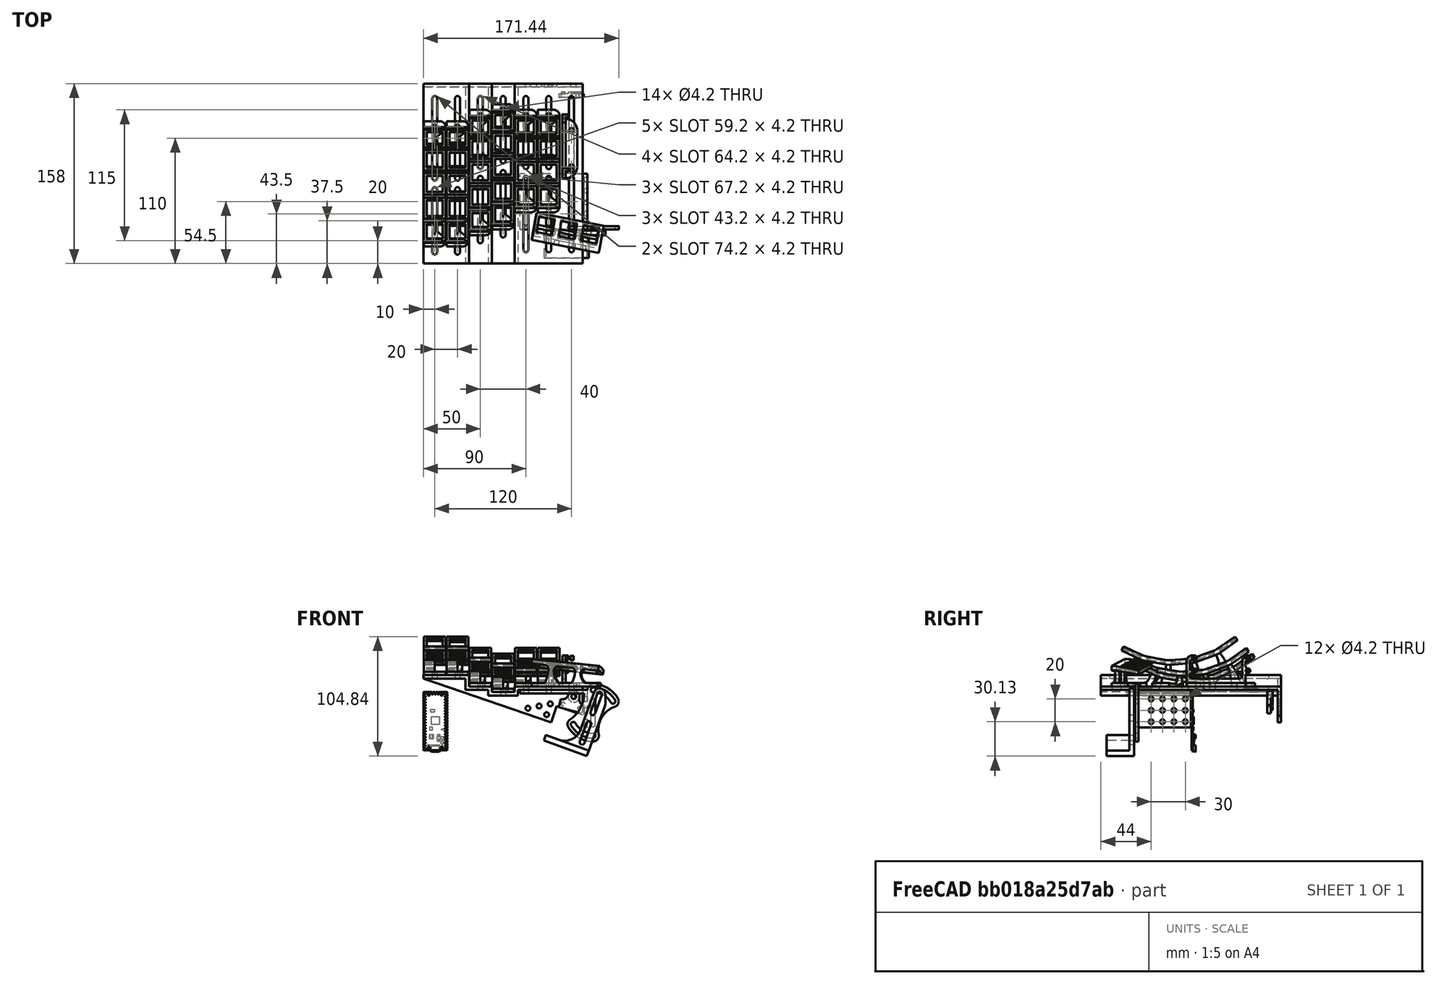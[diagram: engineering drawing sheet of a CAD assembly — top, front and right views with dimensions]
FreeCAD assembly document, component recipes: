
FREECAD ASSEMBLY — COMPONENT RECIPES ("Dactyl Chimera V3")

This assembly document has 15 components, labeled P0..P14 below (a component is one placed body or linked part). 14 of them carry a construction recipe — the FreeCAD feature program that regenerates the part from scratch, quoted from this document or its linked companion documents; the rest are supplied as boundary geometry only. No exploded tour is included for this assembly.
NOTE — document 3 of 4 of this assembly tour. The two overview renders and the header above are repeated from document 1; the component sections below continue where the previous document stopped.
COMPONENT P4 — recipe-attached ("IndexArch", modeled in this document).
Construction recipe (the document's own serialized feature program — sketch geometry with constraints, then the solid features built on it; lengths are millimeters unless a unit is written):

FEATURE [Sketcher::SketchObject] Sketch026
  FullyConstrained = true
  MapMode = 5
  Placement = pos=(0,0,0) rot=(0.57735,0.57735,0.57735;2.0944rad)
  Support = -> [YZ_Plane004]
  expr: Constraints[136] = <<Spreadsheet>>.Wiring
  expr: Constraints[56] = <<Spreadsheet>>.ZRowKey
  expr: Constraints[57] = <<Spreadsheet>>.ARowKey
  expr: Constraints[58] = <<Spreadsheet>>.QRowKey
  expr: Constraints[59] = <<Spreadsheet>>.TopRowKey
  sketch-geometry (49):
    g0: LineSegment StartX=47.4802 StartY=33.7107 StartZ=0 EndX=39.6982 EndY=28.2617 EndZ=0
    g1: LineSegment StartX=39.6982 StartY=28.2617 StartZ=0 EndX=31.9163 EndY=22.8128 EndZ=0
    g2: LineSegment StartX=31.9163 StartY=22.8128 StartZ=0 EndX=29.7273 EndY=21.6733 EndZ=0
    g3: LineSegment StartX=29.7273 StartY=21.6733 StartZ=0 EndX=20.8002 EndY=18.4241 EndZ=0
    g4: LineSegment StartX=20.8002 StartY=18.4241 StartZ=0 EndX=11.8732 EndY=15.1749 EndZ=0
    g5: LineSegment StartX=11.8732 StartY=15.1749 StartZ=0 EndX=9.46385 EndY=14.6407 EndZ=0
    g6: LineSegment StartX=9.46385 StartY=14.6407 StartZ=0 EndX=0 EndY=13.8128 EndZ=0
    g7: LineSegment StartX=0 StartY=13.8128 StartZ=0 EndX=-9.46385 EndY=12.9848 EndZ=0
    g8: LineSegment StartX=-9.46385 StartY=12.9848 StartZ=0 EndX=-11.9293 EndY=13.0924 EndZ=0
    g9: LineSegment StartX=-11.9293 StartY=13.0924 StartZ=0 EndX=-21.285 EndY=14.7421 EndZ=0
    g10: LineSegment StartX=-21.285 StartY=14.7421 StartZ=0 EndX=-30.6407 EndY=16.3917 EndZ=0
    g11: LineSegment StartX=-30.6407 StartY=16.3917 StartZ=0 EndX=-31.3353 EndY=12.4525 EndZ=0
    g12: LineSegment StartX=-31.3353 StartY=12.4525 StartZ=0 EndX=-12.6239 EndY=9.15319 EndZ=0
    g13: LineSegment StartX=-12.6239 StartY=9.15319 StartZ=0 EndX=-9.11523 EndY=9 EndZ=0
    g14: LineSegment StartX=13.2412 StartY=11.4161 StartZ=0 EndX=31.0954 EndY=17.9145 EndZ=0
    g15: LineSegment StartX=31.0954 StartY=17.9145 StartZ=0 EndX=34.2106 EndY=19.5362 EndZ=0
    g16: LineSegment StartX=-9.11523 StartY=9 StartZ=0 EndX=9.81247 EndY=10.656 EndZ=0
    g17: LineSegment StartX=9.81247 StartY=10.656 StartZ=0 EndX=13.2412 EndY=11.4161 EndZ=0
    g18: LineSegment StartX=34.2106 StartY=19.5362 StartZ=0 EndX=49.7745 EndY=30.4341 EndZ=0
    g19: LineSegment StartX=49.7745 StartY=30.4341 StartZ=0 EndX=47.4802 EndY=33.7107 EndZ=0
    g20: LineSegment StartX=31.9163 StartY=22.8128 StartZ=0 EndX=34.2106 EndY=19.5362 EndZ=0
    g21: LineSegment StartX=29.7273 StartY=21.6733 StartZ=0 EndX=31.0954 EndY=17.9145 EndZ=0
    g22: LineSegment StartX=11.8732 StartY=15.1749 StartZ=0 EndX=13.2412 EndY=11.4161 EndZ=0
    g23: LineSegment StartX=9.81247 StartY=10.656 StartZ=0 EndX=9.46385 EndY=14.6407 EndZ=0
    g24: LineSegment StartX=-9.46385 StartY=12.9848 StartZ=0 EndX=-9.11523 EndY=9 EndZ=0
    g25: LineSegment StartX=-12.6239 StartY=9.15319 StartZ=0 EndX=-11.9293 EndY=13.0924 EndZ=0
    g26: LineSegment StartX=-21.285 StartY=14.7421 StartZ=0 EndX=-20.4167 EndY=19.6661 EndZ=0
    g27: LineSegment StartX=-20.4167 StartY=19.6661 StartZ=0 EndX=-17.4623 EndY=19.1452 EndZ=0
    g28: LineSegment StartX=-17.4623 StartY=19.1452 StartZ=0 EndX=-15.7258 EndY=28.9933 EndZ=0
    g29: LineSegment StartX=-4.29592 StartY=28.4942 StartZ=0 EndX=-3.42436 EndY=18.5323 EndZ=0
    g30: LineSegment StartX=-3.42436 StartY=18.5323 StartZ=0 EndX=-0.435779 EndY=18.7937 EndZ=0
    g31: LineSegment StartX=-0.435779 StartY=18.7937 StartZ=0 EndX=0 EndY=13.8128 EndZ=0
    g32: LineSegment StartX=-0.435779 StartY=18.7937 StartZ=0 EndX=2.55281 EndY=19.0552 EndZ=0
    g33: LineSegment StartX=2.55281 StartY=19.0552 StartZ=0 EndX=1.68125 EndY=29.0171 EndZ=0
    g34: LineSegment StartX=12.8509 StartY=31.4934 StartZ=0 EndX=16.2711 EndY=22.0965 EndZ=0
    g35: LineSegment StartX=16.2711 StartY=22.0965 StartZ=0 EndX=19.0901 EndY=23.1225 EndZ=0
    g36: LineSegment StartX=19.0901 StartY=23.1225 StartZ=0 EndX=20.8002 EndY=18.4241 EndZ=0
    g37: LineSegment StartX=19.0901 StartY=23.1225 StartZ=0 EndX=21.9092 EndY=24.1486 EndZ=0
    g38: LineSegment StartX=21.9092 StartY=24.1486 StartZ=0 EndX=18.489 EndY=33.5455 EndZ=0
    g39: LineSegment StartX=28.6371 StartY=38.8283 StartZ=0 EndX=34.3729 EndY=30.6368 EndZ=0
    g40: LineSegment StartX=34.3729 StartY=30.6368 StartZ=0 EndX=36.8304 EndY=32.3575 EndZ=0
    g41: LineSegment StartX=36.8304 StartY=32.3575 StartZ=0 EndX=39.6982 EndY=28.2617 EndZ=0
    g42: ArcOfCircle CenterX=-8.11558 CenterY=72.1532 CenterZ=0 NormalX=0 NormalY=0 NormalZ=1 AngleXU=0 Radius=43.8257 StartAngle=4.53786 EndAngle=4.79966
    g43: ArcOfCircle CenterX=-2.13841 CenterY=72.6761 CenterZ=0 NormalX=0 NormalY=0 NormalZ=1 AngleXU=0 Radius=43.8257 StartAngle=4.79966 EndAngle=5.06145
    g44: ArcOfCircle CenterX=3.49974 CenterY=74.7282 CenterZ=0 NormalX=0 NormalY=0 NormalZ=1 AngleXU=0 Radius=43.8257 StartAngle=5.06145 EndAngle=5.32325
    g45: LineSegment StartX=-50 StartY=3 StartZ=0 EndX=-70 EndY=3 EndZ=0
    g46: LineSegment StartX=-50 StartY=3 StartZ=0 EndX=-50 EndY=9 EndZ=0
    g47: LineSegment StartX=-50 StartY=3 StartZ=0 EndX=-50 EndY=0 EndZ=0
    g48: LineSegment StartX=-50 StartY=9 StartZ=0 EndX=50 EndY=9 EndZ=0
  constraints (142):
    c: Coincident(g0,g1)
    c: Coincident(g1,g2)
    c: Coincident(g2,g3)
    c: Coincident(g3,g4)
    c: Coincident(g4,g5)
    c: Coincident(g5,g6)
    c: Coincident(g6,g7)
    c: Coincident(g7,g8)
    c: Coincident(g8,g9)
    c: Coincident(g9,g10)
    c: Coincident(g10,g11)
    c: Coincident(g11,g12)
    c: Coincident(g12,g13)
    c: Coincident(g14,g15)
    c: Coincident(g13,g16)
    c: Coincident(g16,g17)
    c: Coincident(g17,g14)
    c: Coincident(g15,g18)
    c: Coincident(g18,g19)
    c: Coincident(g19,g0)
    c: Coincident(g20,g1)
    c: Coincident(g20,g15)
    c: Coincident(g21,g2)
    c: Coincident(g21,g14)
    c: Coincident(g22,g4)
    c: Coincident(g22,g14)
    c: Coincident(g23,g16)
    c: Coincident(g23,g5)
    c: Coincident(g24,g7)
    c: Coincident(g24,g13)
    c: Coincident(g25,g12)
    c: Coincident(g25,g8)
    c: Coincident(g9,g26)
    c: Coincident(g26,g27)
    c: Coincident(g27,g28)
    c: Coincident(g29,g30)
    c: Coincident(g30,g31)
    c: Coincident(g31,g6)
    c: Coincident(g30,g32)
    c: Coincident(g32,g33)
    c: Coincident(g34,g35)
    c: Coincident(g35,g36)
    c: Coincident(g36,g3)
    c: Coincident(g35,g37)
    c: Coincident(g37,g38)
    c: Coincident(g39,g40)
    c: Coincident(g40,g41)
    c: Coincident(g0,g41)
    c: Angle(g41,g19) = 0
    c: Angle(g41,g20) = 0
    c: Angle(g21,g36) = 0
    c: Angle(g22,g36) = 0
    c: Angle(g23,g31) = 0
    c: Angle(g24,g31) = 0
    c: Angle(g26,g25) = 0
    c: Angle(g11,g26) = 0
    c: Distance(g26) = 5
    c: Distance(g31) = 5
    c: Distance(g36) = 5
    c: Distance(g41) = 5
    c: Angle(g1,g0) = 3.14159
    c: Angle(g3,g4) = 3.14159
    c: Angle(g6,g7) = 3.14159
    c: Angle(g10,g9) = 3.14159
    c: Perpendicular(g31,g30)
    c: Perpendicular(g30,g29)
    c: Perpendicular(g31,g32)
    c: Perpendicular(g33,g32)
    c: Distance(g16) = 19
    c: Distance(g30,g26) = 20
    c: Distance(g30,g35) = 20
    c: Distance(g35,g40) = 20
    c: Equal(g16,g12)
    c: Equal(g12,g14)
    c: Equal(g14,g18)
    c: Equal(g7,g6)
    c: Equal(g9,g10)
    c: Equal(g3,g4)
    c: Equal(g0,g1)
    c: Distance(g24) = 4
    c: Perpendicular(g31,g7)
    c: Perpendicular(g9,g26)
    c: Perpendicular(g1,g41)
    c: Equal(g20,g21)
    c: Equal(g22,g23)
    c: Equal(g25,g24)
    c: Perpendicular(g24,g16)
    c: Perpendicular(g14,g22)
    c: Perpendicular(g22,g4)
    c: Perpendicular(g20,g18)
    c: Angle(g35,g37) = 3.14159
    c: Perpendicular(g36,g37)
    c: Perpendicular(g37,g38)
    c: Perpendicular(g34,g35)
    c: Perpendicular(g26,g27)
    c: Coincident(g42,g28)
    c: Coincident(g42,g29)
    c: Coincident(g43,g33)
    c: Coincident(g43,g34)
    c: Coincident(g44,g38)
    c: Coincident(g44,g39)
    c: Perpendicular(g44,g38)
    c: Perpendicular(g44,g39)
    c: Perpendicular(g43,g34)
    c: Perpendicular(g43,g33)
    c: Perpendicular(g42,g29)
    c: Perpendicular(g42,g28)
    c: Perpendicular(g27,g28)
    c: Perpendicular(g12,g25)
    c: Equal(g27,g30)
    c: Equal(g30,g32)
    c: Equal(g32,g35)
    c: Equal(g35,g37)
    c: Equal(g37,g40)
    c: Perpendicular(g41,g40)
    c: Distance(g32) = 3
    c: Perpendicular(g39,g40)
    c: Distance(g28) = 10
    c: Distance(g29) = 10
    c: Distance(g33) = 10
    c: Distance(g34) = 10
    c: Distance(g38) = 10
    c: Distance(g39) = 10
    c: Angle(g26,g31) = 0.261799
    c: Angle(g31,g36) = 0.261799
    c: Angle(g36,g41) = 0.261799
    c: Angle(g45,g31) = 1.65806
    c: Coincident(g46,g45)
    c: Vertical(g46)
    c: Coincident(g47,g45)
    c: PointOnObject(g47,g-1)
    c: Vertical(g47)
    c: Coincident(g48,g46)
    c: Horizontal(g48)
    c: Horizontal(g45)
    c: DistanceY(g47,g47) = 3
    c: DistanceY(g46,g46) = 6
    c: DistanceX(g45,g45) = 20
    c: DistanceX(g47,g-1) = 50
    c: DistanceX(g48,g48) = 100
    c: PointOnObject(g6,g-2)
    c: PointOnObject(g13,g48)
FEATURE [PartDesign::Pad] Pad016  label="IArch"
  Direction = (1,-2e-16,3e-16)
  Length = 19
  Length2 = 10
  Midplane = true
  Placement = pos=(0,0,0) rot=(0.57735,0.57735,0.57735;2.0944rad)
  Profile = -> Sketch026
  ReferenceAxis = -> Sketch026 [N_Axis]
  Type = 0
FEATURE [Sketcher::SketchObject] Sketch027
  ExternalGeometry = -> [Sketch026]
  FullyConstrained = true
  MapMode = 5
  Placement = pos=(0,0,0) rot=(0.57735,0.57735,0.57735;2.0944rad)
  Support = -> [YZ_Plane004]
  sketch-geometry (60):
    g0: LineSegment StartX=-21.285 StartY=14.7421 StartZ=0 EndX=-21.9796 EndY=10.8028 EndZ=0
    g1: LineSegment StartX=0 StartY=13.8128 StartZ=0 EndX=0.348623 EndY=9.82798 EndZ=0
    g2: LineSegment StartX=20.8002 StartY=18.4241 StartZ=0 EndX=22.1683 EndY=14.6653 EndZ=0
    g3: LineSegment StartX=39.6982 StartY=28.2617 StartZ=0 EndX=41.9925 EndY=24.9851 EndZ=0
    g4: LineSegment StartX=-28.1786 StartY=15.9576 StartZ=0 EndX=-21.285 EndY=14.7421 EndZ=0
    g5: LineSegment StartX=-21.285 StartY=14.7421 StartZ=0 EndX=-14.3913 EndY=13.5265 EndZ=0
    g6: LineSegment StartX=-14.3913 StartY=13.5265 StartZ=0 EndX=-14.6344 EndY=12.1478 EndZ=0
    g7: LineSegment StartX=-14.6344 StartY=12.1478 StartZ=0 EndX=-13.3542 EndY=11.9221 EndZ=0
    g8: LineSegment StartX=-13.3542 StartY=11.9221 StartZ=0 EndX=-13.8057 EndY=9.36157 EndZ=0
    g9: LineSegment StartX=-13.8057 StartY=9.36157 StartZ=0 EndX=-21.9796 EndY=10.8028 EndZ=0
    g10: LineSegment StartX=-21.9796 StartY=10.8028 StartZ=0 EndX=-30.1535 EndY=12.2441 EndZ=0
    g11: LineSegment StartX=-30.1535 StartY=12.2441 StartZ=0 EndX=-29.702 EndY=14.8046 EndZ=0
    g12: LineSegment StartX=-29.702 StartY=14.8046 StartZ=0 EndX=-28.4217 EndY=14.5789 EndZ=0
    g13: LineSegment StartX=-28.4217 StartY=14.5789 StartZ=0 EndX=-28.1786 EndY=15.9576 EndZ=0
    g14: LineSegment StartX=-29.702 StartY=14.8046 StartZ=0 EndX=-29.4589 EndY=16.1834 EndZ=0
    g15: LineSegment StartX=-13.3542 StartY=11.9221 StartZ=0 EndX=-13.1111 EndY=13.3008 EndZ=0
    g16: LineSegment StartX=-14.6344 StartY=12.1478 StartZ=0 EndX=-15.0859 EndY=9.58731 EndZ=0
    g17: LineSegment StartX=-28.4217 StartY=14.5789 StartZ=0 EndX=-28.8732 EndY=12.0184 EndZ=0
    g18: LineSegment StartX=-6.97336 StartY=13.2027 StartZ=0 EndX=0 EndY=13.8128 EndZ=0
    g19: LineSegment StartX=0 StartY=13.8128 StartZ=0 EndX=6.97336 EndY=14.4228 EndZ=0
    g20: LineSegment StartX=6.97336 StartY=14.4228 StartZ=0 EndX=7.09538 EndY=13.0282 EndZ=0
    g21: LineSegment StartX=7.09538 StartY=13.0282 StartZ=0 EndX=8.39043 EndY=13.1415 EndZ=0
    g22: LineSegment StartX=8.39043 StartY=13.1415 StartZ=0 EndX=8.61704 EndY=10.5514 EndZ=0
    g23: LineSegment StartX=8.61704 StartY=10.5514 StartZ=0 EndX=0.348623 EndY=9.82798 EndZ=0
    g24: LineSegment StartX=0.348623 StartY=9.82798 StartZ=0 EndX=-7.91979 EndY=9.10459 EndZ=0
    g25: LineSegment StartX=-7.91979 StartY=9.10459 StartZ=0 EndX=-8.1464 EndY=11.6947 EndZ=0
    g26: LineSegment StartX=-8.1464 StartY=11.6947 StartZ=0 EndX=-6.85134 EndY=11.808 EndZ=0
    g27: LineSegment StartX=-6.85134 StartY=11.808 StartZ=0 EndX=-6.97336 EndY=13.2027 EndZ=0
    g28: LineSegment StartX=14.2224 StartY=16.0299 StartZ=0 EndX=20.8002 EndY=18.4241 EndZ=0
    g29: LineSegment StartX=20.8002 StartY=18.4241 StartZ=0 EndX=27.3781 EndY=20.8182 EndZ=0
    g30: LineSegment StartX=27.3781 StartY=20.8182 StartZ=0 EndX=27.8569 EndY=19.5026 EndZ=0
    g31: LineSegment StartX=27.8569 StartY=19.5026 StartZ=0 EndX=29.0785 EndY=19.9473 EndZ=0
    g32: LineSegment StartX=29.0785 StartY=19.9473 StartZ=0 EndX=29.9678 EndY=17.5041 EndZ=0
    g33: LineSegment StartX=29.9678 StartY=17.5041 StartZ=0 EndX=22.1683 EndY=14.6653 EndZ=0
    g34: LineSegment StartX=22.1683 StartY=14.6653 StartZ=0 EndX=14.3689 EndY=11.8265 EndZ=0
    g35: LineSegment StartX=14.3689 StartY=11.8265 StartZ=0 EndX=13.4796 EndY=14.2697 EndZ=0
    g36: LineSegment StartX=13.4796 StartY=14.2697 StartZ=0 EndX=14.7012 EndY=14.7144 EndZ=0
    g37: LineSegment StartX=14.7012 StartY=14.7144 StartZ=0 EndX=14.2224 EndY=16.0299 EndZ=0
    g38: LineSegment StartX=33.9642 StartY=24.2467 StartZ=0 EndX=39.6982 EndY=28.2617 EndZ=0
    g39: LineSegment StartX=39.6982 StartY=28.2617 StartZ=0 EndX=45.4323 EndY=32.2768 EndZ=0
    g40: LineSegment StartX=45.4323 StartY=32.2768 StartZ=0 EndX=46.2353 EndY=31.13 EndZ=0
    g41: LineSegment StartX=46.2353 StartY=31.13 StartZ=0 EndX=47.3002 EndY=31.8756 EndZ=0
    g42: LineSegment StartX=47.3002 StartY=31.8756 StartZ=0 EndX=48.7915 EndY=29.7458 EndZ=0
    g43: LineSegment StartX=48.7915 StartY=29.7458 StartZ=0 EndX=41.9925 EndY=24.9851 EndZ=0
    g44: LineSegment StartX=41.9925 StartY=24.9851 StartZ=0 EndX=35.1936 EndY=20.2244 EndZ=0
    g45: LineSegment StartX=35.1936 StartY=20.2244 StartZ=0 EndX=33.7023 EndY=22.3542 EndZ=0
    g46: LineSegment StartX=33.7023 StartY=22.3542 StartZ=0 EndX=34.7672 EndY=23.0999 EndZ=0
    g47: LineSegment StartX=34.7672 StartY=23.0999 StartZ=0 EndX=33.9642 EndY=24.2467 EndZ=0
    g48: LineSegment StartX=-8.1464 StartY=11.6947 StartZ=0 EndX=-8.26842 EndY=13.0894 EndZ=0
    g49: LineSegment StartX=-6.85134 StartY=11.808 StartZ=0 EndX=-6.62474 EndY=9.21789 EndZ=0
    g50: LineSegment StartX=7.09538 StartY=13.0282 StartZ=0 EndX=7.32199 EndY=10.4381 EndZ=0
    g51: LineSegment StartX=8.39043 StartY=13.1415 StartZ=0 EndX=8.26842 EndY=14.5362 EndZ=0
    g52: LineSegment StartX=14.7012 StartY=14.7144 StartZ=0 EndX=15.5905 EndY=12.2711 EndZ=0
    g53: LineSegment StartX=13.4796 StartY=14.2697 StartZ=0 EndX=13.0008 EndY=15.5853 EndZ=0
    g54: LineSegment StartX=27.8569 StartY=19.5026 StartZ=0 EndX=28.7462 EndY=17.0594 EndZ=0
    g55: LineSegment StartX=29.0785 StartY=19.9473 StartZ=0 EndX=28.5997 EndY=21.2628 EndZ=0
    g56: LineSegment StartX=34.7672 StartY=23.0999 StartZ=0 EndX=36.2585 EndY=20.9701 EndZ=0
    g57: LineSegment StartX=33.7023 StartY=22.3542 StartZ=0 EndX=32.8993 EndY=23.5011 EndZ=0
    g58: LineSegment StartX=46.2353 StartY=31.13 StartZ=0 EndX=47.7266 EndY=29.0002 EndZ=0
    g59: LineSegment StartX=47.3002 StartY=31.8756 StartZ=0 EndX=46.4972 EndY=33.0224 EndZ=0
  constraints (172):
    c: Coincident(g0,g-4)
    c: PointOnObject(g0,g-5)
    c: Coincident(g1,g-8)
    c: PointOnObject(g1,g-6)
    c: Coincident(g2,g-10)
    c: PointOnObject(g2,g-11)
    c: Coincident(g3,g-14)
    c: PointOnObject(g3,g-12)
    c: Perpendicular(g-12,g3)
    c: Perpendicular(g-11,g2)
    c: Perpendicular(g-6,g1)
    c: Perpendicular(g-5,g0)
    c: PointOnObject(g4,g-3)
    c: Coincident(g4,g0)
    c: Coincident(g4,g5)
    c: PointOnObject(g5,g-4)
    c: Coincident(g5,g6)
    c: Coincident(g6,g7)
    c: Coincident(g7,g8)
    c: PointOnObject(g8,g-5)
    c: Coincident(g8,g9)
    c: Coincident(g9,g0)
    c: Coincident(g9,g10)
    c: PointOnObject(g10,g-5)
    c: Coincident(g10,g11)
    c: Coincident(g11,g12)
    c: Coincident(g12,g13)
    c: Coincident(g13,g4)
    c: Coincident(g14,g11)
    c: PointOnObject(g14,g-3)
    c: Coincident(g15,g7)
    c: PointOnObject(g15,g-4)
    c: Coincident(g16,g6)
    c: PointOnObject(g16,g9)
    c: Coincident(g17,g12)
    c: PointOnObject(g17,g10)
    c: Angle(g15,g8) = 3.14159
    c: Angle(g16,g6) = 3.14159
    c: Angle(g17,g13) = 3.14159
    c: Angle(g11,g14) = 3.14159
    c: Distance(g8,g10) = 16.6
    c: Distance(g4,g5) = 14
    c: Equal(g5,g4)
    c: Equal(g9,g10)
    c: Perpendicular(g4,g13)
    c: Distance(g13) = 1.4
    c: Equal(g14,g13)
    c: Equal(g13,g6)
    c: Equal(g6,g15)
    c: Perpendicular(g10,g11)
    c: Perpendicular(g5,g6)
    c: Perpendicular(g9,g8)
    c: PointOnObject(g18,g-7)
    c: Coincident(g18,g1)
    c: Coincident(g18,g19)
    c: PointOnObject(g19,g-8)
    c: Coincident(g19,g20)
    c: Coincident(g20,g21)
    c: Coincident(g21,g22)
    c: PointOnObject(g22,g-6)
    c: Coincident(g22,g23)
    c: Coincident(g23,g1)
    c: Coincident(g23,g24)
    c: PointOnObject(g24,g-6)
    c: Coincident(g24,g25)
    c: Coincident(g25,g26)
    c: Coincident(g26,g27)
    c: Coincident(g27,g18)
    c: PointOnObject(g28,g-9)
    c: Coincident(g28,g2)
    c: Coincident(g28,g29)
    c: PointOnObject(g29,g-10)
    c: Coincident(g29,g30)
    c: Coincident(g30,g31)
    c: Coincident(g31,g32)
    c: PointOnObject(g32,g-11)
    c: Coincident(g32,g33)
    c: Coincident(g33,g2)
    c: Coincident(g33,g34)
    c: PointOnObject(g34,g-11)
    c: Coincident(g34,g35)
    c: Coincident(g35,g36)
    c: Coincident(g36,g37)
    c: Coincident(g37,g28)
    c: Coincident(g38,g3)
    c: Coincident(g38,g39)
    c: PointOnObject(g39,g-13)
    c: Coincident(g39,g40)
    c: Coincident(g40,g41)
    c: Coincident(g41,g42)
    c: PointOnObject(g42,g-12)
    c: Coincident(g42,g43)
    c: Coincident(g43,g3)
    c: Coincident(g43,g44)
    c: PointOnObject(g44,g-12)
    c: Coincident(g44,g45)
    c: Coincident(g45,g46)
    c: Coincident(g46,g47)
    c: Coincident(g47,g38)
    c: PointOnObject(g38,g-14)
    c: Equal(g19,g18)
    c: Equal(g28,g29)
    c: Equal(g38,g39)
    c: Equal(g24,g23)
    c: Equal(g34,g33)
    c: Equal(g44,g43)
    c: Distance(g24,g22) = 16.6
    c: Distance(g34,g32) = 16.6
    c: Distance(g44,g42) = 16.6
    c: Distance(g39,g38) = 14
    c: Distance(g29,g28) = 14
    c: Distance(g19,g18) = 14
    c: Coincident(g48,g25)
    c: PointOnObject(g48,g-7)
    c: Coincident(g49,g26)
    c: PointOnObject(g49,g24)
    c: Coincident(g50,g20)
    c: Coincident(g51,g21)
    c: PointOnObject(g51,g-8)
    c: Coincident(g52,g36)
    c: PointOnObject(g52,g34)
    c: Coincident(g53,g35)
    c: PointOnObject(g53,g-9)
    c: PointOnObject(g54,g33)
    c: Coincident(g55,g31)
    c: PointOnObject(g55,g-10)
    c: Coincident(g56,g46)
    c: PointOnObject(g56,g44)
    c: Coincident(g57,g45)
    c: PointOnObject(g57,g-14)
    c: Coincident(g58,g40)
    c: PointOnObject(g58,g43)
    c: Coincident(g59,g41)
    c: PointOnObject(g59,g-13)
    c: Coincident(g54,g30)
    c: Angle(g32,g55) = 3.14159
    c: Angle(g25,g48) = 3.14159
    c: Angle(g27,g49) = 3.14159
    c: Angle(g50,g20) = 3.14159
    c: Angle(g22,g51) = 3.14159
    c: Angle(g35,g53) = 3.14159
    c: Angle(g52,g37) = 3.14159
    c: Angle(g54,g30) = 3.14159
    c: Angle(g45,g57) = 3.14159
    c: Angle(g47,g56) = 3.14159
    c: Angle(g58,g40) = 3.14159
    c: Angle(g42,g59) = 3.14159
    c: Perpendicular(g24,g25)
    c: Perpendicular(g18,g27)
    c: Perpendicular(g19,g20)
    c: Perpendicular(g23,g22)
    c: Perpendicular(g28,g37)
    c: Perpendicular(g34,g35)
    c: Perpendicular(g29,g30)
    c: Perpendicular(g33,g32)
    c: Perpendicular(g44,g45)
    c: Perpendicular(g39,g40)
    c: Perpendicular(g43,g42)
    c: Equal(g59,g40)
    c: Equal(g40,g47)
    c: Equal(g47,g57)
    c: Equal(g55,g30)
    c: Equal(g30,g37)
    c: Equal(g37,g53)
    c: Equal(g51,g20)
    c: Equal(g20,g27)
    c: Equal(g27,g48)
    c: Distance(g48) = 1.4
    c: PointOnObject(g50,g23)
    c: Distance(g53) = 1.4
    c: Distance(g57) = 1.4
    c: Perpendicular(g38,g47)
FEATURE [PartDesign::Pocket] Pocket008  label="IMX Sockets"
  BaseFeature = -> Pad016
  Direction = (-1,2e-16,-3e-16)
  Length = 14
  Length2 = 5
  Midplane = true
  Placement = pos=(0,0,0) rot=(0.57735,0.57735,0.57735;2.0944rad)
  Profile = -> Sketch027
  ReferenceAxis = -> Sketch027 [N_Axis]
  Type = 0
FEATURE [Sketcher::SketchObject] Sketch028
  ExternalGeometry = -> [Sketch027]
  FullyConstrained = true
  MapMode = 5
  Placement = pos=(0,0,0) rot=(0.57735,0.57735,0.57735;2.0944rad)
  Support = -> [YZ_Plane004]
  sketch-geometry (44):
    g0: LineSegment StartX=-21.285 StartY=14.7421 StartZ=0 EndX=-21.4934 EndY=13.5603 EndZ=0
    g1: LineSegment StartX=-21.4934 StartY=13.5603 StartZ=0 EndX=-21.667 EndY=12.5755 EndZ=0
    g2: LineSegment StartX=-21.667 StartY=12.5755 StartZ=0 EndX=-21.9796 EndY=10.8028 EndZ=0
    g3: LineSegment StartX=0 StartY=13.8128 StartZ=0 EndX=0.104587 EndY=12.6173 EndZ=0
    g4: LineSegment StartX=0.104587 StartY=12.6173 StartZ=0 EndX=0.191743 EndY=11.6211 EndZ=0
    g5: LineSegment StartX=0.191743 StartY=11.6211 StartZ=0 EndX=0.348623 EndY=9.82798 EndZ=0
    g6: LineSegment StartX=39.6982 StartY=28.2617 StartZ=0 EndX=40.3865 EndY=27.2788 EndZ=0
    g7: LineSegment StartX=40.3865 StartY=27.2788 StartZ=0 EndX=40.9601 EndY=26.4596 EndZ=0
    g8: LineSegment StartX=40.9601 StartY=26.4596 StartZ=0 EndX=41.9925 EndY=24.9851 EndZ=0
    g9: LineSegment StartX=22.1683 StartY=14.6653 StartZ=0 EndX=21.5527 EndY=16.3567 EndZ=0
    g10: LineSegment StartX=21.5527 StartY=16.3567 StartZ=0 EndX=21.2107 EndY=17.2964 EndZ=0
    g11: LineSegment StartX=21.2107 StartY=17.2964 StartZ=0 EndX=20.8002 EndY=18.4241 EndZ=0
    g12: LineSegment StartX=-28.387 StartY=14.7758 StartZ=0 EndX=-14.5997 EndY=12.3448 EndZ=0
    g13: LineSegment StartX=-14.5997 StartY=12.3448 StartZ=0 EndX=-14.6344 EndY=12.1478 EndZ=0
    g14: LineSegment StartX=-14.6344 StartY=12.1478 StartZ=0 EndX=-13.3542 EndY=11.9221 EndZ=0
    g15: LineSegment StartX=-13.3542 StartY=11.9221 StartZ=0 EndX=-13.4931 EndY=11.1342 EndZ=0
    g16: LineSegment StartX=-13.4931 StartY=11.1342 StartZ=0 EndX=-29.8409 EndY=14.0168 EndZ=0
    g17: LineSegment StartX=-29.8409 StartY=14.0168 StartZ=0 EndX=-29.702 EndY=14.8046 EndZ=0
    g18: LineSegment StartX=-29.702 StartY=14.8046 StartZ=0 EndX=-28.4217 EndY=14.5789 EndZ=0
    g19: LineSegment StartX=-28.4217 StartY=14.5789 StartZ=0 EndX=-28.387 EndY=14.7758 EndZ=0
    g20: LineSegment StartX=-6.86878 StartY=12.0072 StartZ=0 EndX=7.07795 EndY=13.2274 EndZ=0
    g21: LineSegment StartX=7.07795 StartY=13.2274 StartZ=0 EndX=7.09538 EndY=13.0282 EndZ=0
    g22: LineSegment StartX=7.09538 StartY=13.0282 StartZ=0 EndX=8.39043 EndY=13.1415 EndZ=0
    g23: LineSegment StartX=8.39043 StartY=13.1415 StartZ=0 EndX=8.46016 EndY=12.3445 EndZ=0
    g24: LineSegment StartX=8.46016 StartY=12.3445 StartZ=0 EndX=-8.07667 EndY=10.8977 EndZ=0
    g25: LineSegment StartX=-8.07667 StartY=10.8977 StartZ=0 EndX=-8.1464 EndY=11.6947 EndZ=0
    g26: LineSegment StartX=-8.1464 StartY=11.6947 StartZ=0 EndX=-6.85134 EndY=11.808 EndZ=0
    g27: LineSegment StartX=-6.85134 StartY=11.808 StartZ=0 EndX=-6.86878 EndY=12.0072 EndZ=0
    g28: LineSegment StartX=14.6328 StartY=14.9023 StartZ=0 EndX=27.7885 EndY=19.6906 EndZ=0
    g29: LineSegment StartX=27.7885 StartY=19.6906 StartZ=0 EndX=27.8569 EndY=19.5026 EndZ=0
    g30: LineSegment StartX=27.8569 StartY=19.5026 StartZ=0 EndX=29.0785 EndY=19.9473 EndZ=0
    g31: LineSegment StartX=29.0785 StartY=19.9473 StartZ=0 EndX=29.3521 EndY=19.1955 EndZ=0
    g32: LineSegment StartX=29.3521 StartY=19.1955 StartZ=0 EndX=13.7532 EndY=13.518 EndZ=0
    g33: LineSegment StartX=13.7532 StartY=13.518 StartZ=0 EndX=13.4796 EndY=14.2697 EndZ=0
    g34: LineSegment StartX=13.4796 StartY=14.2697 StartZ=0 EndX=14.7012 EndY=14.7144 EndZ=0
    g35: LineSegment StartX=14.7012 StartY=14.7144 StartZ=0 EndX=14.6328 EndY=14.9023 EndZ=0
    g36: LineSegment StartX=34.6525 StartY=23.2637 StartZ=0 EndX=46.1206 EndY=31.2938 EndZ=0
    g37: LineSegment StartX=46.1206 StartY=31.2938 StartZ=0 EndX=46.2353 EndY=31.13 EndZ=0
    g38: LineSegment StartX=46.2353 StartY=31.13 StartZ=0 EndX=47.3002 EndY=31.8756 EndZ=0
    g39: LineSegment StartX=47.3002 StartY=31.8756 StartZ=0 EndX=47.7591 EndY=31.2203 EndZ=0
    g40: LineSegment StartX=47.7591 StartY=31.2203 StartZ=0 EndX=34.1611 EndY=21.6989 EndZ=0
    g41: LineSegment StartX=34.1611 StartY=21.6989 StartZ=0 EndX=33.7023 EndY=22.3542 EndZ=0
    g42: LineSegment StartX=33.7023 StartY=22.3542 StartZ=0 EndX=34.7672 EndY=23.0999 EndZ=0
    g43: LineSegment StartX=34.7672 StartY=23.0999 StartZ=0 EndX=34.6525 EndY=23.2637 EndZ=0
  constraints (112):
    c: Coincident(g-21,g0)
    c: Coincident(g0,g1)
    c: Coincident(g1,g2)
    c: Coincident(g2,g-24)
    c: Coincident(g-16,g3)
    c: Coincident(g3,g4)
    c: Coincident(g4,g5)
    c: Coincident(g5,g-15)
    c: Coincident(g-6,g6)
    c: Coincident(g6,g7)
    c: Coincident(g7,g8)
    c: Coincident(g8,g-3)
    c: Coincident(g-10,g9)
    c: Coincident(g9,g10)
    c: Coincident(g10,g11)
    c: Coincident(g11,g-9)
    c: Angle(g6,g7) = 3.14159
    c: Angle(g8,g7) = 3.14159
    c: Angle(g11,g10) = 3.14159
    c: Angle(g9,g10) = 3.14159
    c: Angle(g3,g4) = 3.14159
    c: Angle(g5,g4) = 3.14159
    c: Angle(g0,g1) = 3.14159
    c: Angle(g2,g1) = 3.14159
    c: PointOnObject(g12,g-26)
    c: PointOnObject(g12,g-22)
    c: Coincident(g12,g13)
    c: Coincident(g13,g-22)
    c: Coincident(g13,g14)
    c: Coincident(g14,g-23)
    c: Coincident(g14,g15)
    c: PointOnObject(g15,g-23)
    c: Coincident(g15,g16)
    c: PointOnObject(g16,g-25)
    c: Coincident(g16,g17)
    c: Coincident(g17,g-25)
    c: Coincident(g17,g18)
    c: Coincident(g18,g-26)
    c: Coincident(g18,g19)
    c: Coincident(g19,g12)
    c: PointOnObject(g20,g-17)
    c: PointOnObject(g20,g-19)
    c: Coincident(g20,g21)
    c: Coincident(g21,g-19)
    c: Coincident(g21,g22)
    c: Coincident(g22,g-20)
    c: Coincident(g22,g23)
    c: PointOnObject(g23,g-20)
    c: Coincident(g23,g24)
    c: PointOnObject(g24,g-18)
    c: Coincident(g24,g25)
    c: Coincident(g25,g-18)
    c: Coincident(g25,g26)
    c: Coincident(g26,g-17)
    c: Coincident(g26,g27)
    c: Coincident(g27,g20)
    c: PointOnObject(g28,g-14)
    c: PointOnObject(g28,g-12)
    c: Coincident(g28,g29)
    c: Coincident(g29,g-12)
    c: Coincident(g29,g30)
    c: Coincident(g30,g-11)
    c: Coincident(g30,g31)
    c: PointOnObject(g31,g-11)
    c: Coincident(g31,g32)
    c: Coincident(g32,g33)
    c: Coincident(g33,g-13)
    c: Coincident(g33,g34)
    c: Coincident(g34,g-14)
    c: Coincident(g34,g35)
    c: Coincident(g35,g28)
    c: PointOnObject(g36,g-7)
    c: PointOnObject(g36,g-4)
    c: Coincident(g36,g37)
    c: Coincident(g37,g-4)
    c: Coincident(g37,g38)
    c: Coincident(g38,g-5)
    c: Coincident(g38,g39)
    c: PointOnObject(g39,g-5)
    c: Coincident(g39,g40)
    c: PointOnObject(g40,g-8)
    c: Coincident(g40,g41)
    c: Coincident(g41,g-8)
    c: Coincident(g41,g42)
    c: Coincident(g42,g-7)
    c: Coincident(g42,g43)
    c: Coincident(g43,g36)
    c: PointOnObject(g32,g-13)
    c: PointOnObject(g1,g16)
    c: PointOnObject(g0,g12)
    c: PointOnObject(g3,g20)
    c: PointOnObject(g4,g24)
    c: PointOnObject(g10,g28)
    c: PointOnObject(g9,g32)
    c: PointOnObject(g6,g36)
    c: PointOnObject(g7,g40)
    c: Perpendicular(g36,g6)
    c: Perpendicular(g8,g40)
    c: Perpendicular(g9,g32)
    c: Perpendicular(g11,g28)
    c: Perpendicular(g3,g20)
    c: Perpendicular(g5,g24)
    c: Perpendicular(g2,g16)
    c: Perpendicular(g0,g12)
    c: Equal(g7,g10)
    c: Equal(g10,g4)
    c: Equal(g4,g1)
    c: Equal(g0,g3)
    c: Equal(g3,g11)
    c: Equal(g11,g6)
    c: Distance(g4) = 1
    c: Distance(g3) = 1.2
FEATURE [PartDesign::Pocket] Pocket009  label="IChoc Sockets"
  BaseFeature = -> Pocket008
  Direction = (-1,2e-16,-3e-16)
  Length = 14.6
  Length2 = 5
  Midplane = true
  Placement = pos=(0,0,0) rot=(0.57735,0.57735,0.57735;2.0944rad)
  Profile = -> Sketch028
  ReferenceAxis = -> Sketch028 [N_Axis]
  Type = 0
FEATURE [Sketcher::SketchObject] Sketch029
  ExternalGeometry = -> [Sketch026]
  FullyConstrained = true
  MapMode = 5
  Placement = pos=(0,0,0) rot=(0.57735,0.57735,0.57735;2.0944rad)
  Support = -> [YZ_Plane004]
  expr: Constraints[18] = <<Spreadsheet>>.Wiring
  sketch-geometry (8):
    g0: LineSegment StartX=9.46385 StartY=14.6407 StartZ=0 EndX=9.81247 EndY=10.656 EndZ=0
    g1: LineSegment StartX=9.81247 StartY=10.656 StartZ=0 EndX=10.3354 EndY=4.67879 EndZ=0
    g2: LineSegment StartX=10.3354 StartY=4.67879 StartZ=0 EndX=10.3354 EndY=0 EndZ=0
    g3: LineSegment StartX=10.3354 StartY=0 StartZ=0 EndX=15.2934 EndY=0 EndZ=0
    g4: LineSegment StartX=15.2934 StartY=0 StartZ=0 EndX=15.2934 EndY=5.77794 EndZ=0
    g5: LineSegment StartX=15.2934 StartY=5.77794 StartZ=0 EndX=13.2412 EndY=11.4161 EndZ=0
    g6: LineSegment StartX=13.2412 StartY=11.4161 StartZ=0 EndX=11.8732 EndY=15.1749 EndZ=0
    g7: LineSegment StartX=9.46385 StartY=14.6407 StartZ=0 EndX=11.8732 EndY=15.1749 EndZ=0
  constraints (20):
    c: Coincident(g-3,g0)
    c: Coincident(g0,g-4)
    c: Coincident(g0,g1)
    c: Coincident(g1,g2)
    c: PointOnObject(g2,g-1)
    c: Vertical(g2)
    c: Coincident(g2,g3)
    c: PointOnObject(g3,g-1)
    c: Coincident(g3,g4)
    c: Vertical(g4)
    c: Coincident(g4,g5)
    c: Coincident(g5,g-4)
    c: Coincident(g5,g6)
    c: Coincident(g6,g-3)
    c: Coincident(g7,g-3)
    c: Coincident(g7,g-3)
    c: Angle(g0,g1) = 3.14159
    c: Angle(g5,g6) = 3.14159
    c: Distance(g1) = 6
    c: Equal(g5,g1)
FEATURE [PartDesign::Pad] Pad017  label="IInner Legs"
  BaseFeature = -> Pocket009
  Direction = (1,-2e-16,3e-16)
  Length = 4.1
  Length2 = 9.5
  Placement = pos=(0,0,0) rot=(0.57735,0.57735,0.57735;2.0944rad)
  Profile = -> Sketch029
  ReferenceAxis = -> Sketch029 [N_Axis]
  Type = 4
  expr: Length = <<Spreadsheet>>.ScrewD / 2 + 2mm
  expr: Length2 = 9.5
FEATURE [Sketcher::SketchObject] Sketch030
  ExternalGeometry = -> [Sketch026]
  FullyConstrained = true
  MapMode = 5
  Placement = pos=(0,0,0) rot=(0.57735,0.57735,0.57735;2.0944rad)
  Support = -> [YZ_Plane004]
  expr: Constraints[32] = <<Spreadsheet>>.Wiring
  expr: Constraints[42] = <<Spreadsheet>>.ArchLength - 10mm
  expr: Constraints[43] = <<Spreadsheet>>.ArchLength - 30mm
  expr: Constraints[44] = <<Spreadsheet>>.ArchLength
  expr: Constraints[45] = <<Spreadsheet>>.ArchLength - 20mm
  expr: Constraints[52] = <<Spreadsheet>>.ArchLength - 25mm
  expr: Constraints[53] = <<Spreadsheet>>.ArchLength - 5mm
  sketch-geometry (36):
    g0: LineSegment StartX=-13.6658 StartY=3.24435 StartZ=0 EndX=-12.6239 EndY=9.15319 EndZ=0
    g1: LineSegment StartX=-12.6239 StartY=9.15319 StartZ=0 EndX=-11.9293 EndY=13.0924 EndZ=0
    g2: LineSegment StartX=-11.9293 StartY=13.0924 StartZ=0 EndX=-9.46385 EndY=12.9848 EndZ=0
    g3: LineSegment StartX=-9.46385 StartY=12.9848 StartZ=0 EndX=-9.11523 EndY=9 EndZ=0
    g4: LineSegment StartX=-15 StartY=0 StartZ=0 EndX=-25 EndY=0 EndZ=0
    g5: LineSegment StartX=-25 StartY=0 StartZ=0 EndX=-25 EndY=3 EndZ=0
    g6: LineSegment StartX=-9.11523 StartY=9 StartZ=0 EndX=-8.59229 EndY=3.02283 EndZ=0
    g7: LineSegment StartX=-8.59229 StartY=3.02283 StartZ=0 EndX=-15 EndY=0 EndZ=0
    g8: LineSegment StartX=37.6521 StartY=14.6212 StartZ=0 EndX=34.2106 EndY=19.5362 EndZ=0
    g9: LineSegment StartX=34.2106 StartY=19.5362 StartZ=0 EndX=31.9163 EndY=22.8128 EndZ=0
    g10: LineSegment StartX=31.9163 StartY=22.8128 StartZ=0 EndX=29.7273 EndY=21.6733 EndZ=0
    g11: LineSegment StartX=29.7273 StartY=21.6733 StartZ=0 EndX=31.0954 EndY=17.9145 EndZ=0
    g12: LineSegment StartX=31.0954 StartY=17.9145 StartZ=0 EndX=33.1475 EndY=12.2763 EndZ=0
    g13: LineSegment StartX=33.1475 StartY=12.2763 StartZ=0 EndX=35 EndY=0 EndZ=0
    g14: LineSegment StartX=35 StartY=0 StartZ=0 EndX=45 EndY=0 EndZ=0
    g15: LineSegment StartX=45 StartY=0 StartZ=0 EndX=45 EndY=3 EndZ=0
    g16: LineSegment StartX=-13.6658 StartY=3.24435 StartZ=0 EndX=-13.9496 EndY=1.63459 EndZ=0
    g17: LineSegment StartX=-13.9496 StartY=1.63459 StartZ=0 EndX=-13.9496 EndY=0 EndZ=0
    g18: LineSegment StartX=45 StartY=3 StartZ=0 EndX=40 EndY=3 EndZ=0
    g19: LineSegment StartX=-25 StartY=3 StartZ=0 EndX=-20 EndY=3 EndZ=0
    g20-g23: Circle x4 (B-spline internal-alignment scaffolding for g24; pole/knot coordinates omitted)
    g24: BSplineCurve PolesCount=4 KnotsCount=2 Degree=3 IsPeriodic=0
    g25: GeomPoint X=-13.6658 Y=3.24435 Z=0
    g26: GeomPoint X=-25 Y=3 Z=0
    g27: LineSegment StartX=37.6521 StartY=14.6212 StartZ=0 EndX=42.2621 EndY=8.03739 EndZ=0
    g28: LineSegment StartX=42.2621 StartY=8.03739 StartZ=0 EndX=42.2621 EndY=0 EndZ=0
    g29-g32: Circle x4 (B-spline internal-alignment scaffolding for g33; pole/knot coordinates omitted)
    g33: BSplineCurve PolesCount=4 KnotsCount=2 Degree=3 IsPeriodic=0
    g34: GeomPoint X=37.6521 Y=14.6212 Z=0
    g35: GeomPoint X=45 Y=3 Z=0
  constraints (82):
    c: Coincident(g0,g-4)
    c: Coincident(g0,g1)
    c: Coincident(g1,g-3)
    c: Coincident(g1,g2)
    c: Coincident(g2,g-3)
    c: Coincident(g2,g3)
    c: Coincident(g3,g-4)
    c: PointOnObject(g4,g-1)
    c: PointOnObject(g4,g-1)
    c: Coincident(g4,g5)
    c: Vertical(g5)
    c: Coincident(g-4,g6)
    c: Coincident(g6,g7)
    c: Coincident(g7,g4)
    c: Coincident(g8,g-6)
    c: Coincident(g8,g9)
    c: Coincident(g9,g-5)
    c: Coincident(g9,g10)
    c: Coincident(g10,g-5)
    c: Coincident(g10,g11)
    c: Coincident(g11,g-6)
    c: Coincident(g11,g12)
    c: Coincident(g12,g13)
    c: PointOnObject(g13,g-1)
    c: Coincident(g13,g14)
    c: PointOnObject(g14,g-1)
    c: Coincident(g14,g15)
    c: Vertical(g15)
    c: Angle(g1,g0) = 3.14159
    c: Angle(g3,g6) = 3.14159
    c: Angle(g11,g12) = 3.14159
    c: Angle(g8,g9) = 3.14159
    c: Distance(g8) = 6
    c: Equal(g8,g12)
    c: Equal(g12,g6)
    c: Equal(g6,g0)
    c: Coincident(g0,g16)
    c: Coincident(g16,g17)
    c: PointOnObject(g17,g-1)
    c: Vertical(g17)
    c: Angle(g0,g16) = 3.14159
    c: Equal(g16,g17)
    c: DistanceX(g-7,g13) = 35
    c: DistanceX(g4,g-7) = 15
    c: DistanceX(g-7,g14) = 45
    c: DistanceX(g4,g-7) = 25
    c: DistanceY(g5,g5) = 3
    c: DistanceY(g15,g15) = 3
    c: Coincident(g18,g15)
    c: Horizontal(g18)
    c: Coincident(g19,g5)
    c: Horizontal(g19)
    c: DistanceX(g19,g-7) = 20
    c: DistanceX(g-7,g18) = 40
    c: Weight(g20) = 1
    c: Coincident(g24,g16)
    c: Equal(g20,g21)
    c: Coincident(g21,g16)
    c: Equal(g20,g22)
    c: Coincident(g22,g19)
    c: Equal(g20,g23)
    c: Coincident(g24,g19)
    c: InternalAlignment(g20-g23 -> g24) x4
    c: InternalAlignment(g25,g24)
    c: InternalAlignment(g26,g24)
    c: Coincident(g8,g27)
    c: Coincident(g27,g28)
    c: PointOnObject(g28,g-1)
    c: Vertical(g28)
    c: Equal(g28,g27)
    c: Angle(g27,g8) = 3.14159
    c: Weight(g29) = 1
    c: Coincident(g33,g27)
    c: Equal(g29,g30)
    c: Coincident(g30,g27)
    c: Equal(g29,g31)
    c: Coincident(g31,g18)
    c: Equal(g29,g32)
    c: Coincident(g33,g18)
    c: InternalAlignment(g29-g32 -> g33) x4
    c: InternalAlignment(g34,g33)
    c: InternalAlignment(g35,g33)
FEATURE [PartDesign::Pad] Pad018  label="IOuter Legs"
  BaseFeature = -> Pad017
  Direction = (1,-2e-16,3e-16)
  Length = 9.5
  Length2 = 10
  Placement = pos=(0,0,0) rot=(0.57735,0.57735,0.57735;2.0944rad)
  Profile = -> Sketch030
  ReferenceAxis = -> Sketch030 [N_Axis]
  Reversed = true
  Type = 0
FEATURE [Sketcher::SketchObject] Sketch031
  ExternalGeometry = -> [Sketch030]
  FullyConstrained = true
  MapMode = 5
  Support = -> [XY_Plane004]
  expr: Constraints[20] = <<Spreadsheet>>.NutR
  expr: Constraints[21] = <<Spreadsheet>>.NutR
  expr: Constraints[26] = <<Spreadsheet>>.ScrewD
  expr: Constraints[46] = <<Spreadsheet>>.ScrewD
  expr: Constraints[47] = <<Spreadsheet>>.NutR
  expr: Constraints[48] = <<Spreadsheet>>.NutR
  sketch-geometry (20):
    g0: LineSegment StartX=7.6225 StartY=-26.0949 StartZ=0 EndX=-3.6e-15 EndY=-20 EndZ=0
    g1: LineSegment StartX=-3.6e-15 StartY=-20 StartZ=0 EndX=-3.3e-15 EndY=-25 EndZ=0
    g2: LineSegment StartX=-3.3e-15 StartY=-25 StartZ=0 EndX=-9.5 EndY=-25 EndZ=0
    g3: LineSegment StartX=-9.5 StartY=-25 StartZ=0 EndX=-9.5 EndY=-35 EndZ=0
    g4: LineSegment StartX=-9.5 StartY=-35 StartZ=0 EndX=4.5 EndY=-35 EndZ=0
    g5: ArcOfCircle CenterX=4.5 CenterY=-30 CenterZ=0 NormalX=0 NormalY=0 NormalZ=1 AngleXU=0 Radius=5 StartAngle=4.71239 EndAngle=7.17949
    g6: LineSegment StartX=-9.5 StartY=-35 StartZ=0 EndX=0 EndY=-30 EndZ=0
    g7: LineSegment StartX=0 StartY=-30 StartZ=0 EndX=9.5 EndY=-35 EndZ=0
    g8: LineSegment StartX=9.5 StartY=-35 StartZ=0 EndX=9.5 EndY=-30 EndZ=0
    g9: Circle CenterX=0 CenterY=-30 CenterZ=0 NormalX=0 NormalY=0 NormalZ=1 AngleXU=0 Radius=2.1
    g10: LineSegment StartX=1.22e-14 StartY=45 StartZ=0 EndX=-9.5 EndY=45 EndZ=0
    g11: LineSegment StartX=-9.5 StartY=45 StartZ=0 EndX=-9.5 EndY=55 EndZ=0
    g12: LineSegment StartX=-9.5 StartY=55 StartZ=0 EndX=4.5 EndY=55 EndZ=0
    g13: ArcOfCircle CenterX=4.5 CenterY=50 CenterZ=0 NormalX=0 NormalY=0 NormalZ=1 AngleXU=0 Radius=5 StartAngle=5.38688 EndAngle=7.85398
    g14: LineSegment StartX=7.6225 StartY=46.0949 StartZ=0 EndX=8.9e-15 EndY=40 EndZ=0
    g15: LineSegment StartX=8.9e-15 StartY=40 StartZ=0 EndX=1.22e-14 EndY=45 EndZ=0
    g16: LineSegment StartX=9.5 StartY=50 StartZ=0 EndX=9.5 EndY=55 EndZ=0
    g17: LineSegment StartX=9.5 StartY=55 StartZ=0 EndX=0 EndY=50 EndZ=0
    g18: LineSegment StartX=0 StartY=50 StartZ=0 EndX=-9.5 EndY=55 EndZ=0
    g19: Circle CenterX=0 CenterY=50 CenterZ=0 NormalX=0 NormalY=0 NormalZ=1 AngleXU=0 Radius=2.1
  constraints (53):
    c: PointOnObject(g0,g-4)
    c: Coincident(g0,g1)
    c: Coincident(g1,g-4)
    c: Coincident(g1,g2)
    c: Horizontal(g2)
    c: Coincident(g2,g3)
    c: Vertical(g3)
    c: Coincident(g3,g4)
    c: Horizontal(g4)
    c: Tangent(g4,g5) = -1.5708
    c: Coincident(g3,g6)
    c: PointOnObject(g6,g-2)
    c: Coincident(g6,g7)
    c: Coincident(g8,g7)
    c: PointOnObject(g8,g5)
    c: Vertical(g8)
    c: Tangent(g8,g5)
    c: Horizontal(g7,g4)
    c: Equal(g7,g6)
    c: DistanceX(g6,g7) = 19
    c: DistanceY(g7,g6) = 5
    c: DistanceY(g6,g-4) = 5
    c: DistanceY(g1,g1) = 5
    c: Coincident(g9,g6)
    c: Horizontal(g5,g6)
    c: Tangent(g5,g0) = -1.5708
    c: Diameter(g9) = 4.2
    c: Coincident(g-3,g10)
    c: Horizontal(g10)
    c: Coincident(g10,g11)
    c: Vertical(g11)
    c: Coincident(g11,g12)
    c: Horizontal(g12)
    c: Tangent(g12,g13) = 1.5708
    c: Tangent(g13,g14) = 1.5708
    c: Coincident(g14,g15)
    c: Coincident(g15,g10)
    c: PointOnObject(g14,g-3)
    c: Vertical(g16)
    c: Coincident(g16,g17)
    c: Coincident(g17,g18)
    c: Coincident(g18,g11)
    c: PointOnObject(g17,g-2)
    c: Equal(g18,g17)
    c: Horizontal(g16,g12)
    c: Coincident(g19,g17)
    c: Diameter(g19) = 4.2
    c: DistanceY(g17,g16) = 5
    c: DistanceY(g-3,g17) = 5
    c: DistanceY(g15,g15) = 5
    c: DistanceX(g18,g16) = 19
    c: Tangent(g16,g13) = -1.5708
    c: Horizontal(g13,g17)
FEATURE [PartDesign::Pad] Pad019  label="IFeet"
  BaseFeature = -> Pad018
  Direction = (0,0,1)
  Length = 3
  Length2 = 10
  Placement = pos=(0,0,0) rot=(0.57735,0.57735,0.57735;2.0944rad)
  Profile = -> Sketch031
  ReferenceAxis = -> Sketch031 [N_Axis]
  Type = 0
FEATURE [PartDesign::Body] Body004  label="IndexArch"
  Group = -> [Sketch026,Pad016,Sketch027,Pocket008,Sketch028,Pocket009,Sketch029,Pad017,Sketch030,Pad018,Sketch031,Pad019]
  Origin = -> Origin004
  Placement = pos=(90,0,5) rot=(0,0,1;0rad)
  Tip = -> Pad019
COMPONENT P5 — recipe-attached ("InnerIndexArch", modeled in this document).
Construction recipe (the document's own serialized feature program — sketch geometry with constraints, then the solid features built on it; lengths are millimeters unless a unit is written):

FEATURE [Sketcher::SketchObject] Sketch032
  FullyConstrained = true
  MapMode = 5
  Placement = pos=(0,0,0) rot=(0.57735,0.57735,0.57735;2.0944rad)
  Support = -> [YZ_Plane005]
  expr: Constraints[104] = <<Spreadsheet>>.ZRowKey
  expr: Constraints[105] = <<Spreadsheet>>.ARowKey
  expr: Constraints[106] = <<Spreadsheet>>.QRowKey
  expr: Constraints[107] = <<Spreadsheet>>.TopRowKey
  expr: Constraints[138] = <<Spreadsheet>>.Wiring
  sketch-geometry (49):
    g0: LineSegment StartX=-31.3353 StartY=12.4525 StartZ=0 EndX=-12.6239 EndY=9.15319 EndZ=0
    g1: LineSegment StartX=-12.6239 StartY=9.15319 StartZ=0 EndX=-9.11523 EndY=9 EndZ=0
    g2: LineSegment StartX=-9.11523 StartY=9 StartZ=0 EndX=9.81247 EndY=10.656 EndZ=0
    g3: LineSegment StartX=9.81247 StartY=10.656 StartZ=0 EndX=13.2412 EndY=11.4161 EndZ=0
    g4: LineSegment StartX=13.2412 StartY=11.4161 StartZ=0 EndX=31.0954 EndY=17.9145 EndZ=0
    g5: LineSegment StartX=31.0954 StartY=17.9145 StartZ=0 EndX=34.2106 EndY=19.5362 EndZ=0
    g6: LineSegment StartX=34.2106 StartY=19.5362 StartZ=0 EndX=49.7745 EndY=30.4341 EndZ=0
    g7: LineSegment StartX=49.7745 StartY=30.4341 StartZ=0 EndX=47.4802 EndY=33.7107 EndZ=0
    g8: LineSegment StartX=47.4802 StartY=33.7107 StartZ=0 EndX=39.6982 EndY=28.2617 EndZ=0
    g9: LineSegment StartX=39.6982 StartY=28.2617 StartZ=0 EndX=31.9163 EndY=22.8128 EndZ=0
    g10: LineSegment StartX=31.9163 StartY=22.8128 StartZ=0 EndX=29.7273 EndY=21.6733 EndZ=0
    g11: LineSegment StartX=29.7273 StartY=21.6733 StartZ=0 EndX=20.8002 EndY=18.4241 EndZ=0
    g12: LineSegment StartX=20.8002 StartY=18.4241 StartZ=0 EndX=11.8732 EndY=15.1749 EndZ=0
    g13: LineSegment StartX=11.8732 StartY=15.1749 StartZ=0 EndX=9.46385 EndY=14.6407 EndZ=0
    g14: LineSegment StartX=9.46385 StartY=14.6407 StartZ=0 EndX=0 EndY=13.8128 EndZ=0
    g15: LineSegment StartX=0 StartY=13.8128 StartZ=0 EndX=-9.46385 EndY=12.9848 EndZ=0
    g16: LineSegment StartX=-9.46385 StartY=12.9848 StartZ=0 EndX=-11.9293 EndY=13.0924 EndZ=0
    g17: LineSegment StartX=-11.9293 StartY=13.0924 StartZ=0 EndX=-21.285 EndY=14.7421 EndZ=0
    g18: LineSegment StartX=-21.285 StartY=14.7421 StartZ=0 EndX=-30.6407 EndY=16.3917 EndZ=0
    g19: LineSegment StartX=-30.6407 StartY=16.3917 StartZ=0 EndX=-31.3353 EndY=12.4525 EndZ=0
    g20: LineSegment StartX=-21.285 StartY=14.7421 StartZ=0 EndX=-20.4167 EndY=19.6661 EndZ=0
    g21: LineSegment StartX=-20.4167 StartY=19.6661 StartZ=0 EndX=-17.4623 EndY=19.1452 EndZ=0
    g22: LineSegment StartX=-17.4623 StartY=19.1452 StartZ=0 EndX=-15.7258 EndY=28.9933 EndZ=0
    g23: LineSegment StartX=-4.29592 StartY=28.4942 StartZ=0 EndX=-3.42436 EndY=18.5323 EndZ=0
    g24: LineSegment StartX=-3.42436 StartY=18.5323 StartZ=0 EndX=-0.435779 EndY=18.7937 EndZ=0
    g25: LineSegment StartX=-0.435779 StartY=18.7937 StartZ=0 EndX=0 EndY=13.8128 EndZ=0
    g26: LineSegment StartX=-0.435779 StartY=18.7937 StartZ=0 EndX=2.55281 EndY=19.0552 EndZ=0
    g27: LineSegment StartX=2.55281 StartY=19.0552 StartZ=0 EndX=1.68125 EndY=29.0171 EndZ=0
    g28: LineSegment StartX=12.8509 StartY=31.4934 StartZ=0 EndX=16.2711 EndY=22.0965 EndZ=0
    g29: LineSegment StartX=16.2711 StartY=22.0965 StartZ=0 EndX=19.0901 EndY=23.1225 EndZ=0
    g30: LineSegment StartX=19.0901 StartY=23.1225 StartZ=0 EndX=20.8002 EndY=18.4241 EndZ=0
    g31: LineSegment StartX=19.0901 StartY=23.1225 StartZ=0 EndX=21.9092 EndY=24.1486 EndZ=0
    g32: LineSegment StartX=21.9092 StartY=24.1486 StartZ=0 EndX=18.489 EndY=33.5455 EndZ=0
    g33: LineSegment StartX=28.6371 StartY=38.8283 StartZ=0 EndX=34.3729 EndY=30.6368 EndZ=0
    g34: LineSegment StartX=34.3729 StartY=30.6368 StartZ=0 EndX=36.8304 EndY=32.3575 EndZ=0
    g35: LineSegment StartX=36.8304 StartY=32.3575 StartZ=0 EndX=39.6982 EndY=28.2617 EndZ=0
    g36: LineSegment StartX=-11.9293 StartY=13.0924 StartZ=0 EndX=-12.6239 EndY=9.15319 EndZ=0
    g37: LineSegment StartX=-9.11523 StartY=9 StartZ=0 EndX=-9.46385 EndY=12.9848 EndZ=0
    g38: LineSegment StartX=9.46385 StartY=14.6407 StartZ=0 EndX=9.81247 EndY=10.656 EndZ=0
    g39: LineSegment StartX=13.2412 StartY=11.4161 StartZ=0 EndX=11.8732 EndY=15.1749 EndZ=0
    g40: LineSegment StartX=29.7273 StartY=21.6733 StartZ=0 EndX=31.0954 EndY=17.9145 EndZ=0
    g41: LineSegment StartX=34.2106 StartY=19.5362 StartZ=0 EndX=31.9163 EndY=22.8128 EndZ=0
    g42: ArcOfCircle CenterX=-8.11558 CenterY=72.1532 CenterZ=0 NormalX=0 NormalY=0 NormalZ=1 AngleXU=0 Radius=43.8257 StartAngle=4.53786 EndAngle=4.79966
    g43: ArcOfCircle CenterX=-2.13841 CenterY=72.6761 CenterZ=0 NormalX=0 NormalY=0 NormalZ=1 AngleXU=0 Radius=43.8257 StartAngle=4.79966 EndAngle=5.06145
    g44: ArcOfCircle CenterX=3.49974 CenterY=74.7282 CenterZ=0 NormalX=0 NormalY=0 NormalZ=1 AngleXU=0 Radius=43.8257 StartAngle=5.06145 EndAngle=5.32325
    g45: LineSegment StartX=-50 StartY=3 StartZ=0 EndX=-70 EndY=3 EndZ=0
    g46: LineSegment StartX=-50 StartY=0 StartZ=0 EndX=-50 EndY=3 EndZ=0
    g47: LineSegment StartX=-50 StartY=3 StartZ=0 EndX=-50 EndY=9 EndZ=0
    g48: LineSegment StartX=-50 StartY=9 StartZ=0 EndX=50 EndY=9 EndZ=0
  constraints (142):
    c: Coincident(g0,g1)
    c: Coincident(g1,g2)
    c: Coincident(g2,g3)
    c: Coincident(g3,g4)
    c: Coincident(g4,g5)
    c: Coincident(g5,g6)
    c: Coincident(g6,g7)
    c: Coincident(g7,g8)
    c: Coincident(g8,g9)
    c: Coincident(g9,g10)
    c: Coincident(g10,g11)
    c: Coincident(g11,g12)
    c: Coincident(g12,g13)
    c: Coincident(g13,g14)
    c: Coincident(g14,g15)
    c: Coincident(g15,g16)
    c: Coincident(g16,g17)
    c: Coincident(g17,g18)
    c: Coincident(g18,g19)
    c: Coincident(g19,g0)
    c: Angle(g18,g17) = 3.14159
    c: Angle(g14,g15) = 3.14159
    c: Angle(g12,g11) = 3.14159
    c: Angle(g9,g8) = 3.14159
    c: Coincident(g17,g20)
    c: Coincident(g20,g21)
    c: Coincident(g21,g22)
    c: Coincident(g23,g24)
    c: Coincident(g24,g25)
    c: Coincident(g25,g14)
    c: Coincident(g24,g26)
    c: Coincident(g26,g27)
    c: Coincident(g28,g29)
    c: Coincident(g29,g30)
    c: Coincident(g30,g11)
    c: Coincident(g29,g31)
    c: Coincident(g31,g32)
    c: Coincident(g33,g34)
    c: Coincident(g34,g35)
    c: Coincident(g35,g8)
    c: Coincident(g36,g16)
    c: Coincident(g36,g0)
    c: Coincident(g37,g1)
    c: Coincident(g37,g15)
    c: Coincident(g38,g13)
    c: Coincident(g38,g2)
    c: Coincident(g39,g3)
    c: Coincident(g39,g12)
    c: Coincident(g40,g10)
    c: Coincident(g40,g4)
    c: Coincident(g41,g5)
    c: Coincident(g41,g9)
    c: Coincident(g42,g23)
    c: Coincident(g43,g27)
    c: Coincident(g43,g28)
    c: Coincident(g44,g32)
    c: Coincident(g44,g33)
    c: Coincident(g42,g22)
    c: Perpendicular(g42,g23)
    c: Perpendicular(g42,g22)
    c: Perpendicular(g43,g27)
    c: Perpendicular(g43,g28)
    c: Perpendicular(g44,g32)
    c: Perpendicular(g44,g33)
    c: Perpendicular(g21,g22)
    c: Perpendicular(g24,g23)
    c: Perpendicular(g26,g27)
    c: Perpendicular(g29,g28)
    c: Perpendicular(g31,g32)
    c: Perpendicular(g34,g33)
    c: Perpendicular(g20,g21)
    c: Perpendicular(g17,g20)
    c: Perpendicular(g15,g25)
    c: Perpendicular(g12,g30)
    c: Perpendicular(g30,g31)
    c: Perpendicular(g35,g34)
    c: Equal(g34,g31)
    c: Equal(g31,g29)
    c: Equal(g29,g26)
    c: Equal(g26,g24)
    c: Equal(g24,g21)
    c: Distance(g24) = 3
    c: Angle(g24,g26) = 3.14159
    c: Angle(g29,g31) = 3.14159
    c: Perpendicular(g9,g35)
    c: Equal(g9,g8)
    c: Perpendicular(g6,g7)
    c: Equal(g41,g40)
    c: Equal(g6,g4)
    c: Equal(g4,g2)
    c: Equal(g2,g0)
    c: Perpendicular(g25,g24)
    c: Equal(g14,g15)
    c: Equal(g17,g18)
    c: Equal(g11,g12)
    c: Distance(g2) = 19
    c: Perpendicular(g37,g2)
    c: Perpendicular(g38,g14)
    c: Perpendicular(g37,g15)
    c: Distance(g37) = 4
    c: Equal(g36,g37)
    c: Perpendicular(g17,g36)
    c: Perpendicular(g0,g19)
    c: Perpendicular(g19,g18)
    c: Distance(g20) = 5
    c: Distance(g25) = 5
    c: Distance(g30) = 5
    c: Distance(g35) = 5
    c: Perpendicular(g6,g41)
    c: Equal(g39,g38)
    c: Perpendicular(g41,g9)
    c: Perpendicular(g4,g39)
    c: Perpendicular(g40,g11)
    c: Perpendicular(g12,g39)
    c: Distance(g33) = 10
    c: Distance(g32) = 10
    c: Distance(g28) = 10
    c: Distance(g27) = 10
    c: Distance(g23) = 10
    c: Distance(g22) = 10
    c: Distance(g24,g20) = 20
    c: Distance(g29,g24) = 20
    c: Distance(g29,g34) = 20
    c: Angle(g20,g25) = 0.261799
    c: Angle(g25,g30) = 0.261799
    c: Angle(g30,g35) = 0.261799
    c: Angle(g45,g25) = 1.65806
    c: Horizontal(g45)
    c: PointOnObject(g46,g-1)
    c: Coincident(g46,g45)
    c: Vertical(g46)
    c: Coincident(g47,g45)
    c: Vertical(g47)
    c: Coincident(g48,g47)
    c: Horizontal(g48)
    c: DistanceX(g48,g48) = 100
    c: DistanceX(g45,g45) = 20
    c: DistanceY(g46,g46) = 3
    c: DistanceY(g47,g47) = 6
    c: DistanceX(g46,g-1) = 50
    c: PointOnObject(g14,g-2)
    c: PointOnObject(g1,g48)
FEATURE [PartDesign::Pad] Pad020  label="IIArch"
  Direction = (1,-2e-16,3e-16)
  Length = 19
  Length2 = 10
  Midplane = true
  Placement = pos=(0,0,0) rot=(0.57735,0.57735,0.57735;2.0944rad)
  Profile = -> Sketch032
  ReferenceAxis = -> Sketch032 [N_Axis]
  Type = 0
FEATURE [Sketcher::SketchObject] Sketch033
  ExternalGeometry = -> [Sketch032]
  FullyConstrained = true
  MapMode = 5
  Placement = pos=(0,0,0) rot=(0.57735,0.57735,0.57735;2.0944rad)
  Support = -> [YZ_Plane005]
  sketch-geometry (60):
    g0: LineSegment StartX=-28.1786 StartY=15.9576 StartZ=0 EndX=-21.285 EndY=14.7421 EndZ=0
    g1: LineSegment StartX=-21.285 StartY=14.7421 StartZ=0 EndX=-14.3913 EndY=13.5265 EndZ=0
    g2: LineSegment StartX=-14.3913 StartY=13.5265 StartZ=0 EndX=-14.6344 EndY=12.1478 EndZ=0
    g3: LineSegment StartX=-14.6344 StartY=12.1478 StartZ=0 EndX=-13.3542 EndY=11.9221 EndZ=0
    g4: LineSegment StartX=-13.3542 StartY=11.9221 StartZ=0 EndX=-13.8057 EndY=9.36157 EndZ=0
    g5: LineSegment StartX=-30.1535 StartY=12.2441 StartZ=0 EndX=-29.702 EndY=14.8046 EndZ=0
    g6: LineSegment StartX=-29.702 StartY=14.8046 StartZ=0 EndX=-28.4217 EndY=14.5789 EndZ=0
    g7: LineSegment StartX=-28.4217 StartY=14.5789 StartZ=0 EndX=-28.1786 EndY=15.9576 EndZ=0
    g8: LineSegment StartX=-6.97336 StartY=13.2027 StartZ=0 EndX=0 EndY=13.8128 EndZ=0
    g9: LineSegment StartX=0 StartY=13.8128 StartZ=0 EndX=6.97336 EndY=14.4228 EndZ=0
    g10: LineSegment StartX=6.97336 StartY=14.4228 StartZ=0 EndX=7.09538 EndY=13.0282 EndZ=0
    g11: LineSegment StartX=7.09538 StartY=13.0282 StartZ=0 EndX=8.39043 EndY=13.1415 EndZ=0
    g12: LineSegment StartX=8.39043 StartY=13.1415 StartZ=0 EndX=8.61704 EndY=10.5514 EndZ=0
    g13: LineSegment StartX=-7.91979 StartY=9.10459 StartZ=0 EndX=-8.1464 EndY=11.6947 EndZ=0
    g14: LineSegment StartX=-8.1464 StartY=11.6947 StartZ=0 EndX=-6.85134 EndY=11.808 EndZ=0
    g15: LineSegment StartX=-6.85134 StartY=11.808 StartZ=0 EndX=-6.97336 EndY=13.2027 EndZ=0
    g16: LineSegment StartX=14.2224 StartY=16.0299 StartZ=0 EndX=20.8002 EndY=18.4241 EndZ=0
    g17: LineSegment StartX=20.8002 StartY=18.4241 StartZ=0 EndX=27.3781 EndY=20.8182 EndZ=0
    g18: LineSegment StartX=27.3781 StartY=20.8182 StartZ=0 EndX=27.8569 EndY=19.5026 EndZ=0
    g19: LineSegment StartX=27.8569 StartY=19.5026 StartZ=0 EndX=29.0785 EndY=19.9473 EndZ=0
    g20: LineSegment StartX=29.0785 StartY=19.9473 StartZ=0 EndX=29.9678 EndY=17.5041 EndZ=0
    g21: LineSegment StartX=14.3689 StartY=11.8265 StartZ=0 EndX=13.4796 EndY=14.2697 EndZ=0
    g22: LineSegment StartX=13.4796 StartY=14.2697 StartZ=0 EndX=14.7012 EndY=14.7144 EndZ=0
    g23: LineSegment StartX=14.7012 StartY=14.7144 StartZ=0 EndX=14.2224 EndY=16.0299 EndZ=0
    g24: LineSegment StartX=33.9642 StartY=24.2467 StartZ=0 EndX=39.6982 EndY=28.2617 EndZ=0
    g25: LineSegment StartX=39.6982 StartY=28.2617 StartZ=0 EndX=45.4323 EndY=32.2768 EndZ=0
    g26: LineSegment StartX=45.4323 StartY=32.2768 StartZ=0 EndX=46.2353 EndY=31.13 EndZ=0
    g27: LineSegment StartX=46.2353 StartY=31.13 StartZ=0 EndX=47.3002 EndY=31.8756 EndZ=0
    g28: LineSegment StartX=47.3002 StartY=31.8756 StartZ=0 EndX=48.7915 EndY=29.7458 EndZ=0
    g29: LineSegment StartX=35.1936 StartY=20.2244 StartZ=0 EndX=33.7023 EndY=22.3542 EndZ=0
    g30: LineSegment StartX=33.7023 StartY=22.3542 StartZ=0 EndX=34.7672 EndY=23.0999 EndZ=0
    g31: LineSegment StartX=34.7672 StartY=23.0999 StartZ=0 EndX=33.9642 EndY=24.2467 EndZ=0
    g32: LineSegment StartX=47.3002 StartY=31.8756 StartZ=0 EndX=46.4972 EndY=33.0224 EndZ=0
    g33: LineSegment StartX=46.2353 StartY=31.13 StartZ=0 EndX=47.7266 EndY=29.0002 EndZ=0
    g34: LineSegment StartX=36.2585 StartY=20.9701 StartZ=0 EndX=34.7672 EndY=23.0999 EndZ=0
    g35: LineSegment StartX=33.7023 StartY=22.3542 StartZ=0 EndX=32.8993 EndY=23.5011 EndZ=0
    g36: LineSegment StartX=28.5997 StartY=21.2628 StartZ=0 EndX=29.0785 EndY=19.9473 EndZ=0
    g37: LineSegment StartX=27.8569 StartY=19.5026 StartZ=0 EndX=28.7462 EndY=17.0594 EndZ=0
    g38: LineSegment StartX=15.5905 StartY=12.2711 StartZ=0 EndX=14.7012 EndY=14.7144 EndZ=0
    g39: LineSegment StartX=13.4796 StartY=14.2697 StartZ=0 EndX=13.0008 EndY=15.5853 EndZ=0
    g40: LineSegment StartX=8.26842 StartY=14.5362 StartZ=0 EndX=8.39043 EndY=13.1415 EndZ=0
    g41: LineSegment StartX=7.09538 StartY=13.0282 StartZ=0 EndX=7.32199 EndY=10.4381 EndZ=0
    g42: LineSegment StartX=-6.85134 StartY=11.808 StartZ=0 EndX=-6.62474 EndY=9.21789 EndZ=0
    g43: LineSegment StartX=-8.1464 StartY=11.6947 StartZ=0 EndX=-8.26842 EndY=13.0894 EndZ=0
    g44: LineSegment StartX=-13.1111 StartY=13.3008 StartZ=0 EndX=-13.3542 EndY=11.9221 EndZ=0
    g45: LineSegment StartX=-14.6344 StartY=12.1478 StartZ=0 EndX=-15.0859 EndY=9.58731 EndZ=0
    g46: LineSegment StartX=-28.8732 StartY=12.0184 StartZ=0 EndX=-28.4217 EndY=14.5789 EndZ=0
    g47: LineSegment StartX=-29.702 StartY=14.8046 StartZ=0 EndX=-29.4589 EndY=16.1834 EndZ=0
    g48: LineSegment StartX=-21.285 StartY=14.7421 StartZ=0 EndX=-21.9796 EndY=10.8028 EndZ=0
    g49: LineSegment StartX=0 StartY=13.8128 StartZ=0 EndX=0.348623 EndY=9.82798 EndZ=0
    g50: LineSegment StartX=39.6982 StartY=28.2617 StartZ=0 EndX=41.9925 EndY=24.9851 EndZ=0
    g51: LineSegment StartX=20.8002 StartY=18.4241 StartZ=0 EndX=22.1683 EndY=14.6653 EndZ=0
    g52: LineSegment StartX=48.7915 StartY=29.7458 StartZ=0 EndX=41.9925 EndY=24.9851 EndZ=0
    g53: LineSegment StartX=41.9925 StartY=24.9851 StartZ=0 EndX=35.1936 EndY=20.2244 EndZ=0
    g54: LineSegment StartX=29.9678 StartY=17.5041 StartZ=0 EndX=22.1683 EndY=14.6653 EndZ=0
    g55: LineSegment StartX=22.1683 StartY=14.6653 StartZ=0 EndX=14.3689 EndY=11.8265 EndZ=0
    g56: LineSegment StartX=8.61704 StartY=10.5514 StartZ=0 EndX=0.348623 EndY=9.82798 EndZ=0
    g57: LineSegment StartX=0.348623 StartY=9.82798 StartZ=0 EndX=-7.91979 EndY=9.10459 EndZ=0
    g58: LineSegment StartX=-13.8057 StartY=9.36157 StartZ=0 EndX=-21.9796 EndY=10.8028 EndZ=0
    g59: LineSegment StartX=-21.9796 StartY=10.8028 StartZ=0 EndX=-30.1535 EndY=12.2441 EndZ=0
  constraints (167):
    c: PointOnObject(g0,g-4)
    c: Coincident(g0,g-4)
    c: Coincident(g0,g1)
    c: Coincident(g1,g2)
    c: Coincident(g2,g3)
    c: Coincident(g3,g4)
    c: PointOnObject(g5,g-5)
    c: Coincident(g5,g6)
    c: Coincident(g6,g7)
    c: Coincident(g7,g0)
    c: PointOnObject(g8,g-6)
    c: Coincident(g8,g-7)
    c: Coincident(g8,g9)
    c: PointOnObject(g9,g-7)
    c: Coincident(g9,g10)
    c: Coincident(g10,g11)
    c: Coincident(g11,g12)
    c: PointOnObject(g13,g-8)
    c: Coincident(g13,g14)
    c: Coincident(g14,g15)
    c: Coincident(g15,g8)
    c: PointOnObject(g16,g-10)
    c: Coincident(g16,g-11)
    c: Coincident(g16,g17)
    c: PointOnObject(g17,g-11)
    c: Coincident(g17,g18)
    c: Coincident(g18,g19)
    c: Coincident(g19,g20)
    c: PointOnObject(g21,g-9)
    c: Coincident(g21,g22)
    c: Coincident(g22,g23)
    c: Coincident(g23,g16)
    c: PointOnObject(g24,g-12)
    c: Coincident(g24,g-13)
    c: Coincident(g24,g25)
    c: PointOnObject(g25,g-13)
    c: Coincident(g25,g26)
    c: Coincident(g26,g27)
    c: Coincident(g27,g28)
    c: PointOnObject(g29,g-14)
    c: Coincident(g29,g30)
    c: Coincident(g30,g31)
    c: Coincident(g31,g24)
    c: Coincident(g32,g27)
    c: PointOnObject(g32,g-13)
    c: Coincident(g33,g26)
    c: Coincident(g34,g30)
    c: PointOnObject(g35,g-12)
    c: PointOnObject(g36,g-11)
    c: Coincident(g36,g19)
    c: Coincident(g37,g18)
    c: Coincident(g38,g22)
    c: Coincident(g39,g21)
    c: PointOnObject(g39,g-10)
    c: PointOnObject(g40,g-7)
    c: Coincident(g40,g11)
    c: Coincident(g41,g10)
    c: Coincident(g42,g14)
    c: Coincident(g43,g13)
    c: PointOnObject(g43,g-6)
    c: PointOnObject(g44,g-3)
    c: Coincident(g44,g3)
    c: Coincident(g45,g2)
    c: Coincident(g46,g6)
    c: Coincident(g47,g5)
    c: PointOnObject(g47,g-4)
    c: Symmetric(g1,g0,g0)
    c: Equal(g47,g7)
    c: Equal(g7,g2)
    c: Equal(g2,g44)
    c: Equal(g44,g43)
    c: Equal(g43,g15)
    c: Equal(g15,g10)
    c: Equal(g10,g40)
    c: Equal(g40,g39)
    c: Equal(g39,g23)
    c: Equal(g23,g18)
    c: Equal(g18,g36)
    c: Equal(g36,g35)
    c: Equal(g35,g31)
    c: Equal(g31,g26)
    c: Equal(g26,g32)
    c: Distance(g40) = 1.4
    c: Distance(g1,g0) = 14
    c: Distance(g5,g4) = 16.6
    c: Coincident(g48,g0)
    c: Perpendicular(g1,g48)
    c: Symmetric(g5,g4,g48)
    c: Angle(g5,g47) = 3.14159
    c: Angle(g7,g46) = 3.14159
    c: Angle(g45,g2) = 3.14159
    c: Angle(g4,g44) = 3.14159
    c: Perpendicular(g0,g7)
    c: Perpendicular(g1,g2)
    c: Coincident(g49,g8)
    c: Perpendicular(g9,g49)
    c: Symmetric(g13,g12,g49)
    c: Coincident(g29,g35)
    c: Angle(g29,g35) = 3.14159
    c: Angle(g31,g34) = 3.14159
    c: Angle(g26,g33) = 3.14159
    c: Angle(g32,g28) = 3.14159
    c: Angle(g36,g20) = 3.14159
    c: Angle(g18,g37) = 3.14159
    c: Angle(g23,g38) = 3.14159
    c: Angle(g21,g39) = 3.14159
    c: Angle(g12,g40) = 3.14159
    c: Angle(g10,g41) = 3.14159
    c: Angle(g42,g15) = 3.14159
    c: Angle(g13,g43) = 3.14159
    c: Equal(g8,g9)
    c: Equal(g9,g16)
    c: Equal(g16,g17)
    c: Equal(g17,g24)
    c: Equal(g24,g25)
    c: Equal(g8,g1)
    c: Coincident(g50,g24)
    c: Coincident(g51,g16)
    c: Perpendicular(g51,g17)
    c: Perpendicular(g50,g25)
    c: Symmetric(g29,g28,g50)
    c: Symmetric(g21,g20,g51)
    c: Perpendicular(g18,g17)
    c: Perpendicular(g16,g23)
    c: Perpendicular(g9,g10)
    c: Perpendicular(g8,g15)
    c: Perpendicular(g24,g31)
    c: Perpendicular(g25,g26)
    c: Coincident(g28,g52)
    c: Coincident(g52,g50)
    c: Coincident(g52,g53)
    c: Coincident(g53,g29)
    c: Coincident(g20,g54)
    c: Coincident(g54,g51)
    c: Coincident(g54,g55)
    c: Coincident(g55,g21)
    c: Coincident(g12,g56)
    c: Coincident(g56,g49)
    c: Coincident(g56,g57)
    c: Coincident(g57,g13)
    c: Coincident(g4,g58)
    c: Coincident(g58,g48)
    c: Coincident(g58,g59)
    c: Coincident(g59,g5)
    c: PointOnObject(g58,g-5)
    c: PointOnObject(g56,g-8)
    c: PointOnObject(g54,g-9)
    c: PointOnObject(g52,g-14)
    c: Distance(g28,g29) = 16.6
    c: Perpendicular(g53,g29)
    c: Perpendicular(g52,g28)
    c: PointOnObject(g33,g52)
    c: PointOnObject(g34,g53)
    c: PointOnObject(g37,g54)
    c: PointOnObject(g38,g55)
    c: PointOnObject(g41,g56)
    c: PointOnObject(g42,g57)
    c: PointOnObject(g45,g58)
    c: PointOnObject(g46,g59)
    c: Perpendicular(g5,g59)
    c: Perpendicular(g58,g4)
    c: Perpendicular(g57,g13)
    c: Distance(g12,g13) = 16.6
    c: Distance(g21,g20) = 16.6
    c: Perpendicular(g56,g12)
    c: Perpendicular(g21,g55)
    c: Perpendicular(g54,g20)
FEATURE [PartDesign::Pocket] Pocket010  label="IIMX Sockets"
  BaseFeature = -> Pad020
  Direction = (-1,2e-16,-3e-16)
  Length = 14
  Length2 = 5
  Midplane = true
  Placement = pos=(0,0,0) rot=(0.57735,0.57735,0.57735;2.0944rad)
  Profile = -> Sketch033
  ReferenceAxis = -> Sketch033 [N_Axis]
  Type = 0
FEATURE [Sketcher::SketchObject] Sketch034
  ExternalGeometry = -> [Sketch033]
  FullyConstrained = true
  MapMode = 5
  Placement = pos=(0,0,0) rot=(0.57735,0.57735,0.57735;2.0944rad)
  Support = -> [YZ_Plane005]
  sketch-geometry (44):
    g0: LineSegment StartX=-21.285 StartY=14.7421 StartZ=0 EndX=-21.4934 EndY=13.5603 EndZ=0
    g1: LineSegment StartX=-21.4934 StartY=13.5603 StartZ=0 EndX=-21.667 EndY=12.5755 EndZ=0
    g2: LineSegment StartX=-21.667 StartY=12.5755 StartZ=0 EndX=-21.9796 EndY=10.8028 EndZ=0
    g3: LineSegment StartX=0 StartY=13.8128 StartZ=0 EndX=0.104587 EndY=12.6173 EndZ=0
    g4: LineSegment StartX=0.104587 StartY=12.6173 StartZ=0 EndX=0.191743 EndY=11.6211 EndZ=0
    g5: LineSegment StartX=0.191743 StartY=11.6211 StartZ=0 EndX=0.348623 EndY=9.82798 EndZ=0
    g6: LineSegment StartX=20.8002 StartY=18.4241 StartZ=0 EndX=21.2107 EndY=17.2964 EndZ=0
    g7: LineSegment StartX=21.2107 StartY=17.2964 StartZ=0 EndX=21.5527 EndY=16.3567 EndZ=0
    g8: LineSegment StartX=21.5527 StartY=16.3567 StartZ=0 EndX=22.1683 EndY=14.6653 EndZ=0
    g9: LineSegment StartX=39.6982 StartY=28.2617 StartZ=0 EndX=40.3865 EndY=27.2788 EndZ=0
    g10: LineSegment StartX=40.3865 StartY=27.2788 StartZ=0 EndX=40.9601 EndY=26.4596 EndZ=0
    g11: LineSegment StartX=40.9601 StartY=26.4596 StartZ=0 EndX=41.9925 EndY=24.9851 EndZ=0
    g12: LineSegment StartX=14.6328 StartY=14.9023 StartZ=0 EndX=27.7885 EndY=19.6906 EndZ=0
    g13: LineSegment StartX=27.7885 StartY=19.6906 StartZ=0 EndX=27.8569 EndY=19.5026 EndZ=0
    g14: LineSegment StartX=27.8569 StartY=19.5026 StartZ=0 EndX=29.0785 EndY=19.9473 EndZ=0
    g15: LineSegment StartX=29.0785 StartY=19.9473 StartZ=0 EndX=29.3521 EndY=19.1955 EndZ=0
    g16: LineSegment StartX=29.3521 StartY=19.1955 StartZ=0 EndX=13.7532 EndY=13.518 EndZ=0
    g17: LineSegment StartX=13.7532 StartY=13.518 StartZ=0 EndX=13.4796 EndY=14.2697 EndZ=0
    g18: LineSegment StartX=13.4796 StartY=14.2697 StartZ=0 EndX=14.7012 EndY=14.7144 EndZ=0
    g19: LineSegment StartX=14.7012 StartY=14.7144 StartZ=0 EndX=14.6328 EndY=14.9023 EndZ=0
    g20: LineSegment StartX=-6.86878 StartY=12.0072 StartZ=0 EndX=7.07795 EndY=13.2274 EndZ=0
    g21: LineSegment StartX=7.07795 StartY=13.2274 StartZ=0 EndX=7.09538 EndY=13.0282 EndZ=0
    g22: LineSegment StartX=7.09538 StartY=13.0282 StartZ=0 EndX=8.39043 EndY=13.1415 EndZ=0
    g23: LineSegment StartX=8.39043 StartY=13.1415 StartZ=0 EndX=8.46016 EndY=12.3445 EndZ=0
    g24: LineSegment StartX=8.46016 StartY=12.3445 StartZ=0 EndX=-8.07667 EndY=10.8977 EndZ=0
    g25: LineSegment StartX=-8.07667 StartY=10.8977 StartZ=0 EndX=-8.1464 EndY=11.6947 EndZ=0
    g26: LineSegment StartX=-8.1464 StartY=11.6947 StartZ=0 EndX=-6.85134 EndY=11.808 EndZ=0
    g27: LineSegment StartX=-6.85134 StartY=11.808 StartZ=0 EndX=-6.86878 EndY=12.0072 EndZ=0
    g28: LineSegment StartX=-28.387 StartY=14.7758 StartZ=0 EndX=-14.5997 EndY=12.3448 EndZ=0
    g29: LineSegment StartX=-14.5997 StartY=12.3448 StartZ=0 EndX=-14.6344 EndY=12.1478 EndZ=0
    g30: LineSegment StartX=-14.6344 StartY=12.1478 StartZ=0 EndX=-13.3542 EndY=11.9221 EndZ=0
    g31: LineSegment StartX=-13.3542 StartY=11.9221 StartZ=0 EndX=-13.4931 EndY=11.1342 EndZ=0
    g32: LineSegment StartX=-13.4931 StartY=11.1342 StartZ=0 EndX=-29.8409 EndY=14.0168 EndZ=0
    g33: LineSegment StartX=-29.8409 StartY=14.0168 StartZ=0 EndX=-29.702 EndY=14.8046 EndZ=0
    g34: LineSegment StartX=-29.702 StartY=14.8046 StartZ=0 EndX=-28.4217 EndY=14.5789 EndZ=0
    g35: LineSegment StartX=-28.4217 StartY=14.5789 StartZ=0 EndX=-28.387 EndY=14.7758 EndZ=0
    g36: LineSegment StartX=34.6525 StartY=23.2637 StartZ=0 EndX=46.1206 EndY=31.2938 EndZ=0
    g37: LineSegment StartX=46.1206 StartY=31.2938 StartZ=0 EndX=46.2353 EndY=31.13 EndZ=0
    g38: LineSegment StartX=46.2353 StartY=31.13 StartZ=0 EndX=47.3002 EndY=31.8756 EndZ=0
    g39: LineSegment StartX=47.3002 StartY=31.8756 StartZ=0 EndX=47.7591 EndY=31.2203 EndZ=0
    g40: LineSegment StartX=47.7591 StartY=31.2203 StartZ=0 EndX=34.1611 EndY=21.6989 EndZ=0
    g41: LineSegment StartX=34.1611 StartY=21.6989 StartZ=0 EndX=33.7023 EndY=22.3542 EndZ=0
    g42: LineSegment StartX=33.7023 StartY=22.3542 StartZ=0 EndX=34.7672 EndY=23.0999 EndZ=0
    g43: LineSegment StartX=34.7672 StartY=23.0999 StartZ=0 EndX=34.6525 EndY=23.2637 EndZ=0
  constraints (112):
    c: Coincident(g-11,g0)
    c: Coincident(g0,g1)
    c: Coincident(g1,g2)
    c: Coincident(g2,g-14)
    c: Coincident(g-7,g3)
    c: Coincident(g3,g4)
    c: Coincident(g4,g5)
    c: Coincident(g5,g-8)
    c: Coincident(g-4,g6)
    c: Coincident(g6,g7)
    c: Coincident(g7,g8)
    c: Coincident(g8,g-6)
    c: Coincident(g-15,g9)
    c: Coincident(g9,g10)
    c: Coincident(g10,g11)
    c: Coincident(g11,g-18)
    c: Angle(g11,g10) = 3.14159
    c: Angle(g9,g10) = 3.14159
    c: Angle(g7,g6) = 3.14159
    c: Angle(g7,g8) = 3.14159
    c: Angle(g4,g3) = 3.14159
    c: Angle(g4,g5) = 3.14159
    c: Angle(g1,g0) = 3.14159
    c: Angle(g1,g2) = 3.14159
    c: Equal(g1,g4)
    c: Equal(g7,g10)
    c: Equal(g7,g4)
    c: PointOnObject(g12,g-3)
    c: PointOnObject(g12,g-22)
    c: Coincident(g12,g13)
    c: Coincident(g13,g-22)
    c: Coincident(g13,g14)
    c: Coincident(g14,g-21)
    c: Coincident(g14,g15)
    c: PointOnObject(g15,g-21)
    c: Coincident(g15,g16)
    c: PointOnObject(g16,g-5)
    c: Coincident(g16,g17)
    c: Coincident(g17,g-5)
    c: Coincident(g17,g18)
    c: Coincident(g18,g-3)
    c: Coincident(g18,g19)
    c: Coincident(g19,g12)
    c: PointOnObject(g6,g12)
    c: PointOnObject(g7,g16)
    c: Perpendicular(g6,g12)
    c: Perpendicular(g8,g16)
    c: PointOnObject(g20,g-10)
    c: PointOnObject(g20,g-23)
    c: Coincident(g20,g21)
    c: Coincident(g21,g22)
    c: Coincident(g22,g-24)
    c: Coincident(g22,g23)
    c: PointOnObject(g23,g-24)
    c: Coincident(g23,g24)
    c: PointOnObject(g24,g-9)
    c: Coincident(g24,g25)
    c: Coincident(g25,g-9)
    c: Coincident(g25,g26)
    c: Coincident(g26,g-10)
    c: Coincident(g26,g27)
    c: Coincident(g27,g20)
    c: Coincident(g-23,g21)
    c: Perpendicular(g3,g20)
    c: Perpendicular(g5,g24)
    c: PointOnObject(g4,g24)
    c: PointOnObject(g3,g20)
    c: PointOnObject(g28,g-25)
    c: Coincident(g28,g29)
    c: Coincident(g29,g-25)
    c: Coincident(g29,g30)
    c: Coincident(g30,g-26)
    c: Coincident(g30,g31)
    c: PointOnObject(g31,g-26)
    c: Coincident(g31,g32)
    c: PointOnObject(g32,g-13)
    c: Coincident(g32,g33)
    c: Coincident(g33,g-13)
    c: Coincident(g33,g34)
    c: Coincident(g34,g-12)
    c: Coincident(g34,g35)
    c: Coincident(g35,g28)
    c: PointOnObject(g28,g-12)
    c: Perpendicular(g0,g28)
    c: Perpendicular(g2,g32)
    c: PointOnObject(g1,g32)
    c: PointOnObject(g0,g28)
    c: Distance(g3) = 1.2
    c: Distance(g4) = 1
    c: Equal(g0,g3)
    c: Equal(g6,g3)
    c: Equal(g9,g3)
    c: PointOnObject(g36,g-16)
    c: PointOnObject(g36,g-19)
    c: Coincident(g36,g37)
    c: Coincident(g37,g-19)
    c: Coincident(g37,g38)
    c: Coincident(g38,g-20)
    c: Coincident(g38,g39)
    c: PointOnObject(g39,g-20)
    c: Coincident(g39,g40)
    c: PointOnObject(g40,g-17)
    c: Coincident(g40,g41)
    c: Coincident(g41,g-17)
    c: Coincident(g41,g42)
    c: Coincident(g42,g-16)
    c: Coincident(g43,g42)
    c: Coincident(g43,g36)
    c: PointOnObject(g9,g36)
    c: PointOnObject(g10,g40)
    c: Perpendicular(g9,g36)
    c: Perpendicular(g11,g40)
FEATURE [PartDesign::Pocket] Pocket011  label="IIChoc Sockets"
  BaseFeature = -> Pocket010
  Direction = (-1,2e-16,-3e-16)
  Length = 14.6
  Length2 = 5
  Midplane = true
  Placement = pos=(0,0,0) rot=(0.57735,0.57735,0.57735;2.0944rad)
  Profile = -> Sketch034
  ReferenceAxis = -> Sketch034 [N_Axis]
  Type = 0
FEATURE [Sketcher::SketchObject] Sketch035
  ExternalGeometry = -> [Sketch032]
  FullyConstrained = true
  MapMode = 5
  Placement = pos=(0,0,0) rot=(0.57735,0.57735,0.57735;2.0944rad)
  Support = -> [YZ_Plane005]
  expr: Constraints[17] = <<Spreadsheet>>.Wiring
  sketch-geometry (8):
    g0: LineSegment StartX=9.46385 StartY=14.6407 StartZ=0 EndX=11.8732 EndY=15.1749 EndZ=0
    g1: LineSegment StartX=11.8732 StartY=15.1749 StartZ=0 EndX=13.2412 EndY=11.4161 EndZ=0
    g2: LineSegment StartX=13.2412 StartY=11.4161 StartZ=0 EndX=15.2934 EndY=5.77794 EndZ=0
    g3: LineSegment StartX=15.2934 StartY=5.77794 StartZ=0 EndX=15.2934 EndY=0 EndZ=0
    g4: LineSegment StartX=15.2934 StartY=0 StartZ=0 EndX=10.3354 EndY=0 EndZ=0
    g5: LineSegment StartX=10.3354 StartY=0 StartZ=0 EndX=10.3354 EndY=4.67879 EndZ=0
    g6: LineSegment StartX=10.3354 StartY=4.67879 StartZ=0 EndX=9.81247 EndY=10.656 EndZ=0
    g7: LineSegment StartX=9.81247 StartY=10.656 StartZ=0 EndX=9.46385 EndY=14.6407 EndZ=0
  constraints (20):
    c: Coincident(g-3,g0)
    c: Coincident(g0,g-3)
    c: Coincident(g0,g1)
    c: Coincident(g1,g-4)
    c: Coincident(g1,g2)
    c: Coincident(g2,g3)
    c: PointOnObject(g3,g-1)
    c: Vertical(g3)
    c: Coincident(g3,g4)
    c: PointOnObject(g4,g-1)
    c: Coincident(g4,g5)
    c: Vertical(g5)
    c: Coincident(g5,g6)
    c: Coincident(g6,g-4)
    c: Coincident(g6,g7)
    c: Coincident(g7,g0)
    c: Equal(g2,g6)
    c: Distance(g6) = 6
    c: Angle(g6,g7) = 3.14159
    c: Angle(g2,g1) = 3.14159
FEATURE [PartDesign::Pad] Pad021  label="IIInner Legs"
  BaseFeature = -> Pocket011
  Direction = (1,-2e-16,3e-16)
  Length = 4.1
  Length2 = 9.5
  Placement = pos=(0,0,0) rot=(0.57735,0.57735,0.57735;2.0944rad)
  Profile = -> Sketch035
  ReferenceAxis = -> Sketch035 [N_Axis]
  Type = 4
  expr: Length = <<Spreadsheet>>.ScrewD / 2 + 2mm
FEATURE [Sketcher::SketchObject] Sketch036
  ExternalGeometry = -> [Sketch032]
  FullyConstrained = true
  MapMode = 5
  Placement = pos=(0,0,0) rot=(0.57735,0.57735,0.57735;2.0944rad)
  Support = -> [YZ_Plane005]
  expr: Constraints[22] = <<Spreadsheet>>.ArchLength - 30mm
  expr: Constraints[23] = <<Spreadsheet>>.ArchLength - 25mm
  expr: Constraints[24] = <<Spreadsheet>>.ArchLength - 20mm
  expr: Constraints[71] = <<Spreadsheet>>.ArchLength
  expr: Constraints[72] = <<Spreadsheet>>.ArchLength - 5mm
  expr: Constraints[73] = <<Spreadsheet>>.ArchLength - 10mm
  sketch-geometry (36):
    g0: LineSegment StartX=-11.9293 StartY=13.0924 StartZ=0 EndX=-9.46385 EndY=12.9848 EndZ=0
    g1: LineSegment StartX=-9.46385 StartY=12.9848 StartZ=0 EndX=-9.11523 EndY=9 EndZ=0
    g2: LineSegment StartX=-9.11523 StartY=9 StartZ=0 EndX=-8.59229 EndY=3.02283 EndZ=0
    g3: LineSegment StartX=-8.59229 StartY=3.02283 StartZ=0 EndX=-15 EndY=0 EndZ=0
    g4: LineSegment StartX=-15 StartY=0 StartZ=0 EndX=-25 EndY=0 EndZ=0
    g5: LineSegment StartX=-25 StartY=0 StartZ=0 EndX=-25 EndY=3 EndZ=0
    g6: LineSegment StartX=-11.9293 StartY=13.0924 StartZ=0 EndX=-12.6239 EndY=9.15319 EndZ=0
    g7: LineSegment StartX=-12.6239 StartY=9.15319 StartZ=0 EndX=-13.6658 EndY=3.24435 EndZ=0
    g8: LineSegment StartX=-13.6658 StartY=3.24435 StartZ=0 EndX=-13.9496 EndY=1.63459 EndZ=0
    g9: LineSegment StartX=-25 StartY=3 StartZ=0 EndX=-20 EndY=3 EndZ=0
    g10: LineSegment StartX=37.6521 StartY=14.6212 StartZ=0 EndX=34.2106 EndY=19.5362 EndZ=0
    g11: LineSegment StartX=34.2106 StartY=19.5362 StartZ=0 EndX=31.9163 EndY=22.8128 EndZ=0
    g12: LineSegment StartX=31.9163 StartY=22.8128 StartZ=0 EndX=29.7273 EndY=21.6733 EndZ=0
    g13: LineSegment StartX=29.7273 StartY=21.6733 StartZ=0 EndX=31.0954 EndY=17.9145 EndZ=0
    g14: LineSegment StartX=31.0954 StartY=17.9145 StartZ=0 EndX=33.1475 EndY=12.2763 EndZ=0
    g15: LineSegment StartX=33.1475 StartY=12.2763 StartZ=0 EndX=35 EndY=0 EndZ=0
    g16: LineSegment StartX=35 StartY=0 StartZ=0 EndX=45 EndY=0 EndZ=0
    g17: LineSegment StartX=45 StartY=0 StartZ=0 EndX=45 EndY=3 EndZ=0
    g18: LineSegment StartX=45 StartY=3 StartZ=0 EndX=40 EndY=3 EndZ=0
    g19: LineSegment StartX=42.2621 StartY=8.03739 StartZ=0 EndX=37.6521 EndY=14.6212 EndZ=0
    g20: LineSegment StartX=-13.9496 StartY=1.63459 StartZ=0 EndX=-13.9496 EndY=0 EndZ=0
    g21-g24: Circle x4 (B-spline internal-alignment scaffolding for g25; pole/knot coordinates omitted)
    g25: BSplineCurve PolesCount=4 KnotsCount=2 Degree=3 IsPeriodic=0
    g26: GeomPoint X=-13.6658 Y=3.24435 Z=0
    g27: GeomPoint X=-25 Y=3 Z=0
    g28: LineSegment StartX=42.2621 StartY=8.03739 StartZ=0 EndX=42.2621 EndY=0 EndZ=0
    g29-g32: Circle x4 (B-spline internal-alignment scaffolding for g33; pole/knot coordinates omitted)
    g33: BSplineCurve PolesCount=4 KnotsCount=2 Degree=3 IsPeriodic=0
    g34: GeomPoint X=37.6521 Y=14.6212 Z=0
    g35: GeomPoint X=45 Y=3 Z=0
  constraints (82):
    c: Coincident(g-5,g0)
    c: Coincident(g0,g-5)
    c: Coincident(g0,g1)
    c: Coincident(g1,g-6)
    c: Coincident(g1,g2)
    c: Coincident(g2,g3)
    c: PointOnObject(g3,g-1)
    c: Coincident(g3,g4)
    c: PointOnObject(g4,g-1)
    c: Coincident(g4,g5)
    c: Vertical(g5)
    c: Coincident(g0,g6)
    c: Coincident(g6,g-6)
    c: Coincident(g7,g6)
    c: Distance(g7) = 6
    c: Equal(g2,g7)
    c: Coincident(g7,g8)
    c: Horizontal(g9)
    c: Angle(g7,g8) = 3.14159
    c: Angle(g6,g7) = 3.14159
    c: Angle(g2,g1) = 3.14159
    c: DistanceY(g5,g5) = 3
    c: DistanceX(g3,g-7) = 15
    c: DistanceX(g9,g-7) = 20
    c: DistanceX(g4,g-7) = 25
    c: Coincident(g10,g-4)
    c: Coincident(g10,g11)
    c: Coincident(g11,g-3)
    c: Coincident(g11,g12)
    c: Coincident(g12,g-3)
    c: Coincident(g12,g13)
    c: Coincident(g13,g-4)
    c: Coincident(g13,g14)
    c: Coincident(g14,g15)
    c: PointOnObject(g15,g-1)
    c: Coincident(g15,g16)
    c: PointOnObject(g16,g-1)
    c: Coincident(g16,g17)
    c: Vertical(g17)
    c: Coincident(g19,g10)
    c: Horizontal(g18)
    c: Angle(g19,g10) = 3.14159
    c: Angle(g14,g13) = 3.14159
    c: Angle(g10,g11) = 3.14159
    c: Equal(g10,g14)
    c: Equal(g10,g7)
    c: Coincident(g9,g5)
    c: Coincident(g20,g8)
    c: PointOnObject(g20,g-1)
    c: Vertical(g20)
    c: Equal(g20,g8)
    c: Weight(g21) = 1
    c: Coincident(g25,g7)
    c: Equal(g21,g22)
    c: Coincident(g22,g8)
    c: Equal(g21,g23)
    c: Coincident(g23,g9)
    c: Equal(g21,g24)
    c: Coincident(g25,g5)
    c: InternalAlignment(g21-g24 -> g25) x4
    c: InternalAlignment(g26,g25)
    c: InternalAlignment(g27,g25)
    c: Coincident(g28,g19)
    c: PointOnObject(g28,g-1)
    c: Vertical(g28)
    c: Equal(g28,g19)
    c: Coincident(g18,g17)
    c: Equal(g17,g5)
    c: DistanceX(g-7,g17) = 45
    c: DistanceX(g-7,g18) = 40
    c: DistanceX(g-7,g15) = 35
    c: Weight(g29) = 1
    c: Coincident(g33,g10)
    c: Equal(g29,g30)
    c: Coincident(g30,g19)
    c: Equal(g29,g31)
    c: Coincident(g31,g18)
    c: Equal(g29,g32)
    c: Coincident(g33,g17)
    c: InternalAlignment(g29-g32 -> g33) x4
    c: InternalAlignment(g34,g33)
    c: InternalAlignment(g35,g33)
FEATURE [PartDesign::Pad] Pad022  label="IIOuter Legs"
  BaseFeature = -> Pad021
  Direction = (1,-2e-16,3e-16)
  Length = 9.5
  Length2 = 10
  Placement = pos=(0,0,0) rot=(0.57735,0.57735,0.57735;2.0944rad)
  Profile = -> Sketch036
  ReferenceAxis = -> Sketch036 [N_Axis]
  Reversed = true
  Type = 0
FEATURE [Sketcher::SketchObject] Sketch037
  ExternalGeometry = -> [Sketch036]
  FullyConstrained = true
  MapMode = 5
  Support = -> [XY_Plane005]
  expr: Constraints[19] = <<Spreadsheet>>.NutR
  expr: Constraints[20] = <<Spreadsheet>>.NutR
  expr: Constraints[25] = <<Spreadsheet>>.ScrewD
  expr: Constraints[59] = <<Spreadsheet>>.ScrewD
  expr: Constraints[60] = <<Spreadsheet>>.NutR
  expr: Constraints[61] = <<Spreadsheet>>.NutR
  sketch-geometry (24):
    g0: LineSegment StartX=-4.4e-15 StartY=-20 StartZ=0 EndX=7.6225 EndY=-26.0949 EndZ=0
    g1: LineSegment StartX=-4.4e-15 StartY=-20 StartZ=0 EndX=-5.6e-15 EndY=-25 EndZ=0
    g2: LineSegment StartX=-5.6e-15 StartY=-25 StartZ=0 EndX=-9.5 EndY=-25 EndZ=0
    g3: LineSegment StartX=-9.5 StartY=-25 StartZ=0 EndX=-9.5 EndY=-35 EndZ=0
    g4: LineSegment StartX=-9.5 StartY=-35 StartZ=0 EndX=4.5 EndY=-35 EndZ=0
    g5: ArcOfCircle CenterX=4.5 CenterY=-30 CenterZ=0 NormalX=0 NormalY=0 NormalZ=1 AngleXU=0 Radius=5 StartAngle=4.71239 EndAngle=7.17949
    g6: LineSegment StartX=4.5 StartY=-35 StartZ=0 EndX=9.5 EndY=-35 EndZ=0
    g7: LineSegment StartX=9.5 StartY=-35 StartZ=0 EndX=9.5 EndY=-30 EndZ=0
    g8: Circle CenterX=0 CenterY=-30 CenterZ=0 NormalX=0 NormalY=0 NormalZ=1 AngleXU=0 Radius=2.1
    g9: LineSegment StartX=0 StartY=-30 StartZ=0 EndX=9.5 EndY=-30 EndZ=0
    g10: LineSegment StartX=9.5 StartY=-35 StartZ=0 EndX=0 EndY=-30 EndZ=0
    g11: LineSegment StartX=0 StartY=-30 StartZ=0 EndX=-9.5 EndY=-35 EndZ=0
    g12: LineSegment StartX=1e-14 StartY=45 StartZ=0 EndX=8.9e-15 EndY=40 EndZ=0
    g13: LineSegment StartX=-9.5 StartY=45 StartZ=0 EndX=-9.5 EndY=55 EndZ=0
    g14: LineSegment StartX=-9.5 StartY=55 StartZ=0 EndX=4.5 EndY=55 EndZ=0
    g15: ArcOfCircle CenterX=4.5 CenterY=50 CenterZ=0 NormalX=0 NormalY=0 NormalZ=1 AngleXU=0 Radius=5 StartAngle=5.38688 EndAngle=7.85398
    g16: LineSegment StartX=7.6225 StartY=46.0949 StartZ=0 EndX=8.9e-15 EndY=40 EndZ=0
    g17: LineSegment StartX=1e-14 StartY=45 StartZ=0 EndX=-9.5 EndY=45 EndZ=0
    g18: LineSegment StartX=4.5 StartY=55 StartZ=0 EndX=9.5 EndY=55 EndZ=0
    g19: LineSegment StartX=9.5 StartY=55 StartZ=0 EndX=9.5 EndY=50 EndZ=0
    g20: LineSegment StartX=9.5 StartY=55 StartZ=0 EndX=0 EndY=50 EndZ=0
    g21: LineSegment StartX=0 StartY=50 StartZ=0 EndX=-9.5 EndY=55 EndZ=0
    g22: LineSegment StartX=0 StartY=50 StartZ=0 EndX=9.5 EndY=50 EndZ=0
    g23: Circle CenterX=0 CenterY=50 CenterZ=0 NormalX=0 NormalY=0 NormalZ=1 AngleXU=0 Radius=2.1
  constraints (62):
    c: PointOnObject(g0,g-4)
    c: Coincident(g0,g1)
    c: Coincident(g1,g-4)
    c: Coincident(g1,g2)
    c: Horizontal(g2)
    c: Coincident(g2,g3)
    c: Vertical(g3)
    c: Coincident(g3,g4)
    c: Horizontal(g4)
    c: Tangent(g5,g0) = 1.5708
    c: Tangent(g5,g4) = -1.5708
    c: Coincident(g4,g6)
    c: Horizontal(g6)
    c: Coincident(g6,g7)
    c: PointOnObject(g7,g5)
    c: Vertical(g7)
    c: DistanceX(g3,g6) = 19
    c: DistanceY(g1,g1) = 5
    c: PointOnObject(g8,g-2)
    c: DistanceY(g8,g1) = 5
    c: DistanceY(g3,g8) = 5
    c: Coincident(g9,g8)
    c: Coincident(g9,g7)
    c: Horizontal(g9)
    c: PointOnObject(g5,g9)
    c: Diameter(g8) = 4.2
    c: Coincident(g6,g10)
    c: Coincident(g10,g8)
    c: Coincident(g10,g11)
    c: Coincident(g11,g3)
    c: Equal(g11,g10)
    c: Coincident(g-3,g12)
    c: PointOnObject(g12,g-3)
    c: Vertical(g13)
    c: Coincident(g13,g14)
    c: Horizontal(g14)
    c: Tangent(g14,g15) = 1.5708
    c: Tangent(g15,g16) = 1.5708
    c: Coincident(g16,g12)
    c: Coincident(g17,g12)
    c: Coincident(g17,g13)
    c: Equal(g12,g1)
    c: Coincident(g14,g18)
    c: Coincident(g18,g19)
    c: Vertical(g19)
    c: PointOnObject(g19,g15)
    c: Horizontal(g18)
    c: DistanceX(g13,g18) = 19
    c: Horizontal(g17)
    c: Coincident(g18,g20)
    c: PointOnObject(g20,g-2)
    c: Coincident(g20,g21)
    c: Coincident(g21,g13)
    c: Equal(g20,g21)
    c: Coincident(g22,g20)
    c: Coincident(g22,g19)
    c: Horizontal(g22)
    c: PointOnObject(g15,g22)
    c: Coincident(g23,g20)
    c: Diameter(g23) = 4.2
    c: DistanceY(g12,g23) = 5
    c: DistanceY(g23,g13) = 5
FEATURE [PartDesign::Pad] Pad023
  BaseFeature = -> Pad022
  Direction = (0,0,1)
  Length = 3
  Length2 = 10
  Placement = pos=(0,0,0) rot=(0.57735,0.57735,0.57735;2.0944rad)
  Profile = -> Sketch037
  ReferenceAxis = -> Sketch037 [N_Axis]
  Type = 0
FEATURE [PartDesign::Body] Body005  label="InnerIndexArch"
  Group = -> [Sketch032,Pad020,Sketch033,Pocket010,Sketch034,Pocket011,Sketch035,Pad021,Sketch036,Pad022,Sketch037,Pad023]
  Origin = -> Origin005
  Placement = pos=(110,0,5) rot=(0,0,1;0rad)
  Tip = -> Pad023
  expr: .Placement.Base.y = <<IndexArch>>.Placement.Base.y
  expr: .Placement.Base.z = <<IndexArch>>.Placement.Base.z
COMPONENT P6 — recipe-attached ("BasePlate", modeled in this document).
Construction recipe (the document's own serialized feature program — sketch geometry with constraints, then the solid features built on it; lengths are millimeters unless a unit is written):

FEATURE [Sketcher::SketchObject] Sketch038
  FullyConstrained = true
  MapMode = 5
  Placement = pos=(0,0,0) rot=(1,0,0;1.5708rad)
  Support = -> [XZ_Plane007]
  expr: Constraints[33] = <<OuterArch>>.Placement.Base.z
  expr: Constraints[38] = <<RingArch>>.Placement.Base.z
  expr: Constraints[39] = <<IndexArch>>.Placement.Base.z
  expr: Constraints[53] = 20mm + <<MiddleArch>>.Placement.Base.z
  sketch-geometry (18):
    g0: LineSegment StartX=0 StartY=15 StartZ=0 EndX=40 EndY=15 EndZ=0
    g1: LineSegment StartX=40 StartY=15 StartZ=0 EndX=40 EndY=5 EndZ=0
    g2: LineSegment StartX=40 StartY=5 StartZ=0 EndX=60 EndY=5 EndZ=0
    g3: LineSegment StartX=60 StartY=5 StartZ=0 EndX=60 EndY=0 EndZ=0
    g4: LineSegment StartX=60 StartY=0 StartZ=0 EndX=80 EndY=0 EndZ=0
    g5: LineSegment StartX=80 StartY=0 StartZ=0 EndX=80 EndY=5 EndZ=0
    g6: LineSegment StartX=80 StartY=5 StartZ=0 EndX=140 EndY=5 EndZ=0
    g7: LineSegment StartX=140 StartY=5 StartZ=0 EndX=140 EndY=2 EndZ=0
    g8: LineSegment StartX=140 StartY=2 StartZ=0 EndX=83 EndY=2 EndZ=0
    g9: LineSegment StartX=83 StartY=2 StartZ=0 EndX=83 EndY=-3 EndZ=0
    g10: LineSegment StartX=83 StartY=-3 StartZ=0 EndX=57 EndY=-3 EndZ=0
    g11: LineSegment StartX=57 StartY=-3 StartZ=0 EndX=57 EndY=2 EndZ=0
    g12: LineSegment StartX=57 StartY=2 StartZ=0 EndX=37 EndY=2 EndZ=0
    g13: LineSegment StartX=37 StartY=2 StartZ=0 EndX=37 EndY=12 EndZ=0
    g14: LineSegment StartX=37 StartY=12 StartZ=0 EndX=0 EndY=12 EndZ=0
    g15: LineSegment StartX=0 StartY=12 StartZ=0 EndX=0 EndY=15 EndZ=0
    g16: LineSegment StartX=0 StartY=-20 StartZ=0 EndX=60 EndY=-20 EndZ=0
    g17: LineSegment StartX=60 StartY=0 StartZ=0 EndX=60 EndY=-20 EndZ=0
  constraints (54):
    c: PointOnObject(g0,g-2)
    c: Horizontal(g0)
    c: Coincident(g0,g1)
    c: Coincident(g1,g2)
    c: Horizontal(g2)
    c: Coincident(g2,g3)
    c: Coincident(g3,g4)
    c: Horizontal(g4)
    c: Coincident(g4,g5)
    c: Vertical(g5)
    c: Coincident(g5,g6)
    c: Horizontal(g6)
    c: Coincident(g6,g7)
    c: Vertical(g7)
    c: Coincident(g7,g8)
    c: Horizontal(g8)
    c: Coincident(g8,g9)
    c: Vertical(g9)
    c: Coincident(g9,g10)
    c: Horizontal(g10)
    c: Coincident(g10,g11)
    c: Coincident(g11,g12)
    c: Horizontal(g12)
    c: Coincident(g12,g13)
    c: Vertical(g13)
    c: Coincident(g13,g14)
    c: Horizontal(g14)
    c: Coincident(g14,g15)
    c: Coincident(g15,g0)
    c: PointOnObject(g14,g-2)
    c: Vertical(g1)
    c: Vertical(g3)
    c: Vertical(g11)
    c: DistanceY(g-1,g0) = 15
    c: DistanceX(g0,g0) = 40
    c: DistanceX(g-1,g2) = 60
    c: DistanceX(g-1,g5) = 80
    c: DistanceX(g-1,g6) = 140
    c: DistanceY(g-1,g1) = 5
    c: DistanceY(g-1,g5) = 5
    c: DistanceY(g15,g15) = 3
    c: DistanceY(g12,g1) = 3
    c: DistanceX(g12,g1) = 3
    c: DistanceX(g11,g3) = 3
    c: DistanceY(g10,g3) = 3
    c: DistanceY(g7,g7) = 3
    c: DistanceX(g4,g8) = 3
    c: PointOnObject(g16,g-2)
    c: Horizontal(g16)
    c: Coincident(g17,g3)
    c: Coincident(g17,g16)
    c: Vertical(g17)
    c: DistanceY(g16,g-1) = 20
    c: DistanceY(g17,g17) = 20
FEATURE [PartDesign::Pad] Pad024  label="Plate"
  Direction = (0,-1,-2e-16)
  Length = 80
  Length2 = 78
  Placement = pos=(0,0,0) rot=(1,0,0;1.5708rad)
  Profile = -> Sketch038
  ReferenceAxis = -> Sketch038 [N_Axis]
  Type = 4
  expr: Length = -<<OuterArch>>.Placement.Base.y + <<Spreadsheet>>.ArchLength + <<Spreadsheet>>.NutR * 3 + 10mm
  expr: Length2 = <<MiddleArch>>.Placement.Base.y + <<Spreadsheet>>.ArchLength + <<Spreadsheet>>.NutR * 3 + 13mm
FEATURE [Sketcher::SketchObject] Sketch039
  ExternalGeometry = -> [Sketch038]
  FullyConstrained = true
  MapMode = 5
  Placement = pos=(0,78,0) rot=(-1,0,0;1.5708rad)
  Support = -> [Pad024]
  expr: Constraints[20] = <<Spreadsheet>>.ScrewD
  expr: Constraints[36] = <<Spreadsheet>>.NutR + 1mm
  expr: Constraints[62] = <<Spreadsheet>>.NutR * 2
  expr: Constraints[71] = <<Spreadsheet>>.NutR
  sketch-geometry (29):
    g0: LineSegment StartX=140 StartY=-5 StartZ=0 EndX=140 EndY=20.1125 EndZ=0
    g1: LineSegment StartX=0 StartY=-12 StartZ=0 EndX=0 EndY=-15 EndZ=0
    g2: LineSegment StartX=0 StartY=-15 StartZ=0 EndX=40 EndY=-15 EndZ=0
    g3: LineSegment StartX=40 StartY=-15 StartZ=0 EndX=40 EndY=-5 EndZ=0
    g4: LineSegment StartX=40 StartY=-5 StartZ=0 EndX=60 EndY=-5 EndZ=0
    g5: LineSegment StartX=60 StartY=-5 StartZ=0 EndX=60 EndY=0 EndZ=0
    g6: LineSegment StartX=60 StartY=0 StartZ=0 EndX=80 EndY=-4e-16 EndZ=0
    g7: LineSegment StartX=80 StartY=-4e-16 StartZ=0 EndX=80 EndY=-5 EndZ=0
    g8: LineSegment StartX=80 StartY=-5 StartZ=0 EndX=140 EndY=-5 EndZ=0
    g9: Circle CenterX=131.539 CenterY=4 CenterZ=0 NormalX=0 NormalY=0 NormalZ=1 AngleXU=0 Radius=2.1
    g10: LineSegment StartX=131.539 StartY=4 StartZ=0 EndX=140 EndY=4 EndZ=0
    g11: LineSegment StartX=131.539 StartY=4 StartZ=0 EndX=129.594 EndY=9.67607 EndZ=0
    g12: LineSegment StartX=140 StartY=20.1125 StartZ=0 EndX=117.081 EndY=12.2597 EndZ=0
    g13: LineSegment StartX=112.219 StartY=26.4498 StartZ=0 EndX=0 EndY=-12 EndZ=0
    g14: LineSegment StartX=131.539 StartY=4 StartZ=0 EndX=131.539 EndY=-2 EndZ=0
    g15: LineSegment StartX=140 StartY=13.2415 StartZ=0 EndX=119.188 EndY=6.11059 EndZ=0
    g16: LineSegment StartX=119.188 StartY=6.11059 StartZ=0 EndX=117.081 EndY=12.2597 EndZ=0
    g17: LineSegment StartX=117.081 StartY=12.2597 StartZ=0 EndX=112.219 EndY=26.4498 EndZ=0
    g18: LineSegment StartX=106.543 StartY=24.505 StartZ=0 EndX=108.163 EndY=19.775 EndZ=0
    g19: LineSegment StartX=108.163 StartY=19.775 StartZ=0 EndX=111.405 EndY=10.3149 EndZ=0
    g20: LineSegment StartX=91.7781 StartY=14.1608 StartZ=0 EndX=90.1574 EndY=18.8909 EndZ=0
    g21: Circle CenterX=111.405 CenterY=10.3149 CenterZ=0 NormalX=0 NormalY=0 NormalZ=1 AngleXU=0 Radius=2.1
    g22: Circle CenterX=108.163 CenterY=19.775 CenterZ=0 NormalX=0 NormalY=0 NormalZ=1 AngleXU=0 Radius=2.1
    g23: Circle CenterX=91.7781 CenterY=14.1608 CenterZ=0 NormalX=0 NormalY=0 NormalZ=1 AngleXU=0 Radius=2.1
    g24: LineSegment StartX=111.405 StartY=10.3149 StartZ=0 EndX=117.081 EndY=12.2597 EndZ=0
    g25: LineSegment StartX=108.163 StartY=19.775 StartZ=0 EndX=101.591 EndY=12.2378 EndZ=0
    g26: LineSegment StartX=101.591 StartY=12.2378 StartZ=0 EndX=91.7781 EndY=14.1608 EndZ=0
    g27: LineSegment StartX=101.591 StartY=12.2378 StartZ=0 EndX=111.405 EndY=10.3149 EndZ=0
    g28: Circle CenterX=101.591 CenterY=12.2378 CenterZ=0 NormalX=0 NormalY=0 NormalZ=1 AngleXU=0 Radius=2.1
  constraints (72):
    c: Coincident(g-9,g0)
    c: Vertical(g0)
    c: Coincident(g0,g12)
    c: Coincident(g13,g-4)
    c: Coincident(g13,g1)
    c: Coincident(g1,g-3)
    c: Coincident(g1,g2)
    c: Coincident(g2,g-3)
    c: Coincident(g2,g3)
    c: Coincident(g3,g-6)
    c: Coincident(g3,g4)
    c: Coincident(g4,g-6)
    c: Coincident(g4,g5)
    c: Coincident(g5,g-8)
    c: Coincident(g5,g6)
    c: Coincident(g6,g-8)
    c: Coincident(g6,g7)
    c: Coincident(g7,g-9)
    c: Coincident(g7,g8)
    c: Coincident(g8,g0)
    c: Diameter(g9) = 4.2
    c: Coincident(g10,g9)
    c: PointOnObject(g10,g0)
    c: Horizontal(g10)
    c: Coincident(g11,g9)
    c: Coincident(g17,g13)
    c: Coincident(g14,g9)
    c: PointOnObject(g14,g-10)
    c: Vertical(g14)
    c: PointOnObject(g15,g0)
    c: Coincident(g16,g15)
    c: Coincident(g16,g17)
    c: Distance(g16,g17) = 21.5
    c: Coincident(g16,g12)
    c: Distance(g16) = 6.5
    c: PointOnObject(g11,g15)
    c: DistanceY(g14,g14) = 6
    c: Equal(g14,g11)
    c: Distance(g15) = 22
    c: Symmetric(g15,g15,g11)
    c: Angle(g17,g16) = 3.14159
    c: Parallel(g12,g13)
    c: Perpendicular(g15,g16)
    c: Perpendicular(g17,g12)
    c: PointOnObject(g18,g13)
    c: Coincident(g18,g19)
    c: PointOnObject(g20,g13)
    c: PointOnObject(g24,g19)
    c: Angle(g19,g18) = 3.14159
    c: Perpendicular(g13,g20)
    c: Perpendicular(g18,g13)
    c: Coincident(g21,g19)
    c: Coincident(g22,g18)
    c: Equal(g23,g22)
    c: Equal(g21,g9)
    c: Equal(g22,g9)
    c: Tangent(g24,g12) = 1.5708
    c: Equal(g24,g14)
    c: Coincident(g25,g22)
    c: Coincident(g26,g23)
    c: Coincident(g27,g25)
    c: Coincident(g27,g21)
    c: Distance(g27) = 10
    c: Coincident(g25,g26)
    c: Equal(g25,g26)
    c: Coincident(g28,g25)
    c: Coincident(g23,g20)
    c: Equal(g26,g27)
    c: Equal(g19,g27)
    c: Equal(g28,g21)
    c: Equal(g20,g18)
    c: Distance(g18) = 5
FEATURE [PartDesign::Pad] Pad025
  BaseFeature = -> Pad024
  Direction = (0,1,2e-16)
  Length = 3
  Length2 = 10
  Placement = pos=(0,0,0) rot=(1,0,0;1.5708rad)
  Profile = -> Sketch039
  ReferenceAxis = -> Sketch039 [N_Axis]
  Reversed = true
  Type = 0
FEATURE [Sketcher::SketchObject] Sketch048
  FullyConstrained = true
  MapMode = 5
  Support = -> [XY_Plane007]
  expr: .Constraints.Rlyy = -<<Thumb Cluster>>.Placement.Base.y + 7mm
  expr: Constraints[112] = <<Spreadsheet>>.NutR * 2
  expr: Constraints[113] = <<Spreadsheet>>.ScrewD
  expr: Constraints[149] = <<Spreadsheet>>.ArchLength + <<MiddleArch>>.Placement.Base.y + <<Spreadsheet>>.NutR + 10mm
  expr: Constraints[152] = <<OuterArch>>.Placement.Base.y + <<Spreadsheet>>.NutR
  expr: Constraints[153] = <<PinkieArch>>.Placement.Base.y + <<Spreadsheet>>.NutR
  expr: Constraints[154] = <<Spreadsheet>>.ArchLength + -<<OuterArch>>.Placement.Base.y + <<Spreadsheet>>.NutR + 10mm
  expr: Constraints[155] = <<RingArch>>.Placement.Base.y + <<Spreadsheet>>.NutR
  expr: Constraints[156] = <<Spreadsheet>>.ArchLength + -<<PinkieArch>>.Placement.Base.y + <<Spreadsheet>>.NutR + 10mm
  expr: Constraints[157] = <<MiddleArch>>.Placement.Base.y + <<Spreadsheet>>.NutR
  expr: Constraints[158] = <<IndexArch>>.Placement.Base.y + <<Spreadsheet>>.NutR
  expr: Constraints[159] = <<InnerIndexArch>>.Placement.Base.y + <<Spreadsheet>>.NutR
  expr: Constraints[161] = <<Spreadsheet>>.ArchLength + -<<RingArch>>.Placement.Base.y + <<Spreadsheet>>.NutR + 10mm
  expr: Constraints[162] = <<Spreadsheet>>.ArchLength + -<<MiddleArch>>.Placement.Base.y + <<Spreadsheet>>.NutR + 10mm
  sketch-geometry (70):
    g0: ArcOfCircle CenterX=10 CenterY=-5 CenterZ=0 NormalX=0 NormalY=0 NormalZ=1 AngleXU=0 Radius=2.1 StartAngle=3.14159 EndAngle=6.28319
    g1: ArcOfCircle CenterX=10 CenterY=65 CenterZ=0 NormalX=0 NormalY=0 NormalZ=1 AngleXU=0 Radius=2.1 StartAngle=3.2e-15 EndAngle=3.14159
    g2: LineSegment StartX=12.1 StartY=-5 StartZ=0 EndX=12.1 EndY=65 EndZ=0
    g3: LineSegment StartX=7.9 StartY=65 StartZ=0 EndX=7.9 EndY=-5 EndZ=0
    g4: ArcOfCircle CenterX=10 CenterY=-15 CenterZ=0 NormalX=0 NormalY=0 NormalZ=1 AngleXU=0 Radius=2.1 StartAngle=3e-16 EndAngle=3.14159
    g5: ArcOfCircle CenterX=10 CenterY=-70 CenterZ=0 NormalX=0 NormalY=0 NormalZ=1 AngleXU=0 Radius=2.1 StartAngle=3.14159 EndAngle=6.28319
    g6: LineSegment StartX=7.9 StartY=-15 StartZ=0 EndX=7.9 EndY=-70 EndZ=0
    g7: LineSegment StartX=12.1 StartY=-70 StartZ=0 EndX=12.1 EndY=-15 EndZ=0
    g8: ArcOfCircle CenterX=30 CenterY=-70 CenterZ=0 NormalX=0 NormalY=0 NormalZ=1 AngleXU=0 Radius=2.1 StartAngle=3.14159 EndAngle=6.28319
    g9: ArcOfCircle CenterX=30 CenterY=-15 CenterZ=0 NormalX=0 NormalY=0 NormalZ=1 AngleXU=0 Radius=2.1 StartAngle=3e-16 EndAngle=3.14159
    g10: LineSegment StartX=32.1 StartY=-70 StartZ=0 EndX=32.1 EndY=-15 EndZ=0
    g11: LineSegment StartX=27.9 StartY=-15 StartZ=0 EndX=27.9 EndY=-70 EndZ=0
    g12: ArcOfCircle CenterX=50 CenterY=-5 CenterZ=0 NormalX=0 NormalY=0 NormalZ=1 AngleXU=0 Radius=2.1 StartAngle=0 EndAngle=3.14159
    g13: ArcOfCircle CenterX=50 CenterY=-60 CenterZ=0 NormalX=0 NormalY=0 NormalZ=1 AngleXU=0 Radius=2.1 StartAngle=3.14159 EndAngle=6.28319
    g14: LineSegment StartX=47.9 StartY=-5 StartZ=0 EndX=47.9 EndY=-60 EndZ=0
    g15: LineSegment StartX=52.1 StartY=-60 StartZ=0 EndX=52.1 EndY=-5 EndZ=0
    g16: ArcOfCircle CenterX=70 CenterY=-55 CenterZ=0 NormalX=0 NormalY=0 NormalZ=1 AngleXU=0 Radius=2.1 StartAngle=3.14159 EndAngle=6.28319
    g17: ArcOfCircle CenterX=70 CenterY=5e-16 CenterZ=0 NormalX=0 NormalY=0 NormalZ=1 AngleXU=0 Radius=2.1 StartAngle=0 EndAngle=3.14159
    g18: LineSegment StartX=72.1 StartY=-55 StartZ=0 EndX=72.1 EndY=0 EndZ=0
    g19: LineSegment StartX=67.9 StartY=8e-16 StartZ=0 EndX=67.9 EndY=-55 EndZ=0
    g20: ArcOfCircle CenterX=90 CenterY=-68 CenterZ=0 NormalX=0 NormalY=0 NormalZ=1 AngleXU=0 Radius=2.1 StartAngle=3.14159 EndAngle=6.28319
    g21: ArcOfCircle CenterX=90 CenterY=-5 CenterZ=0 NormalX=0 NormalY=0 NormalZ=1 AngleXU=0 Radius=2.1 StartAngle=1e-16 EndAngle=3.14159
    g22: LineSegment StartX=92.1 StartY=-68 StartZ=0 EndX=92.1 EndY=-5 EndZ=0
    g23: LineSegment StartX=87.9 StartY=-5 StartZ=0 EndX=87.9 EndY=-68 EndZ=0
    g24: ArcOfCircle CenterX=110 CenterY=-5 CenterZ=0 NormalX=0 NormalY=0 NormalZ=1 AngleXU=0 Radius=2.1 StartAngle=2e-16 EndAngle=3.14159
    g25: ArcOfCircle CenterX=110 CenterY=-68 CenterZ=0 NormalX=0 NormalY=0 NormalZ=1 AngleXU=0 Radius=2.1 StartAngle=3.14159 EndAngle=6.28319
    g26: LineSegment StartX=107.9 StartY=-5 StartZ=0 EndX=107.9 EndY=-68 EndZ=0
    g27: LineSegment StartX=112.1 StartY=-68 StartZ=0 EndX=112.1 EndY=-5 EndZ=0
    g28: ArcOfCircle CenterX=130 CenterY=-68 CenterZ=0 NormalX=0 NormalY=0 NormalZ=1 AngleXU=0 Radius=2.1 StartAngle=3.14159 EndAngle=6.28319
    g29: ArcOfCircle CenterX=130 CenterY=-5 CenterZ=0 NormalX=0 NormalY=0 NormalZ=1 AngleXU=0 Radius=2.1 StartAngle=1e-16 EndAngle=3.14159
    g30: LineSegment StartX=132.1 StartY=-68 StartZ=0 EndX=132.1 EndY=-5 EndZ=0
    g31: LineSegment StartX=127.9 StartY=-5 StartZ=0 EndX=127.9 EndY=-68 EndZ=0
    g32: ArcOfCircle CenterX=130 CenterY=5 CenterZ=0 NormalX=0 NormalY=0 NormalZ=1 AngleXU=0 Radius=2.1 StartAngle=3.14159 EndAngle=6.28319
    g33: ArcOfCircle CenterX=130 CenterY=65 CenterZ=0 NormalX=0 NormalY=0 NormalZ=1 AngleXU=0 Radius=2.1 StartAngle=-9e-16 EndAngle=3.14159
    g34: LineSegment StartX=132.1 StartY=5 StartZ=0 EndX=132.1 EndY=65 EndZ=0
    g35: LineSegment StartX=127.9 StartY=65 StartZ=0 EndX=127.9 EndY=5 EndZ=0
    g36: ArcOfCircle CenterX=110 CenterY=65 CenterZ=0 NormalX=0 NormalY=0 NormalZ=1 AngleXU=0 Radius=2.1 StartAngle=-1.8e-15 EndAngle=3.14159
    g37: ArcOfCircle CenterX=110 CenterY=5 CenterZ=0 NormalX=0 NormalY=0 NormalZ=1 AngleXU=0 Radius=2.1 StartAngle=3.14159 EndAngle=6.28319
    g38: LineSegment StartX=107.9 StartY=65 StartZ=0 EndX=107.9 EndY=5 EndZ=0
    g39: LineSegment StartX=112.1 StartY=5 StartZ=0 EndX=112.1 EndY=65 EndZ=0
    g40: ArcOfCircle CenterX=90 CenterY=5 CenterZ=0 NormalX=0 NormalY=0 NormalZ=1 AngleXU=0 Radius=2.1 StartAngle=3.14159 EndAngle=6.28319
    g41: ArcOfCircle CenterX=90 CenterY=65 CenterZ=0 NormalX=0 NormalY=0 NormalZ=1 AngleXU=0 Radius=2.1 StartAngle=-9e-16 EndAngle=3.14159
    g42: LineSegment StartX=92.1 StartY=5 StartZ=0 EndX=92.1 EndY=65 EndZ=0
    g43: LineSegment StartX=87.9 StartY=65 StartZ=0 EndX=87.9 EndY=5 EndZ=0
    g44: ArcOfCircle CenterX=70 CenterY=10 CenterZ=0 NormalX=0 NormalY=0 NormalZ=1 AngleXU=0 Radius=2.1 StartAngle=3.14159 EndAngle=6.28319
    g45: ArcOfCircle CenterX=70 CenterY=65 CenterZ=0 NormalX=0 NormalY=0 NormalZ=1 AngleXU=0 Radius=2.1 StartAngle=-2.7e-15 EndAngle=3.14159
    g46: LineSegment StartX=72.1 StartY=10 StartZ=0 EndX=72.1 EndY=65 EndZ=0
    g47: LineSegment StartX=67.9 StartY=65 StartZ=0 EndX=67.9 EndY=10 EndZ=0
    g48: ArcOfCircle CenterX=50 CenterY=5 CenterZ=0 NormalX=0 NormalY=0 NormalZ=1 AngleXU=0 Radius=2.1 StartAngle=3.14159 EndAngle=6.28319
    g49: ArcOfCircle CenterX=50 CenterY=65 CenterZ=0 NormalX=0 NormalY=0 NormalZ=1 AngleXU=0 Radius=2.1 StartAngle=5e-16 EndAngle=3.14159
    g50: LineSegment StartX=52.1 StartY=5 StartZ=0 EndX=52.1 EndY=65 EndZ=0
    g51: LineSegment StartX=47.9 StartY=65 StartZ=0 EndX=47.9 EndY=5 EndZ=0
    g52: ArcOfCircle CenterX=30 CenterY=-5 CenterZ=0 NormalX=0 NormalY=0 NormalZ=1 AngleXU=0 Radius=2.1 StartAngle=3.14159 EndAngle=6.28319
    g53: ArcOfCircle CenterX=30 CenterY=65 CenterZ=0 NormalX=0 NormalY=0 NormalZ=1 AngleXU=0 Radius=2.1 StartAngle=-9e-16 EndAngle=3.14159
    g54: LineSegment StartX=32.1 StartY=-5 StartZ=0 EndX=32.1 EndY=65 EndZ=0
    g55: LineSegment StartX=27.9 StartY=65 StartZ=0 EndX=27.9 EndY=-5 EndZ=0
    g56: LineSegment StartX=10 StartY=65 StartZ=0 EndX=30 EndY=65 EndZ=0
    g57: LineSegment StartX=30 StartY=65 StartZ=0 EndX=50 EndY=65 EndZ=0
    g58: LineSegment StartX=50 StartY=65 StartZ=0 EndX=70 EndY=65 EndZ=0
    g59: LineSegment StartX=70 StartY=65 StartZ=0 EndX=90 EndY=65 EndZ=0
    g60: LineSegment StartX=90 StartY=65 StartZ=0 EndX=110 EndY=65 EndZ=0
    g61: LineSegment StartX=110 StartY=65 StartZ=0 EndX=130 EndY=65 EndZ=0
    g62: LineSegment StartX=10 StartY=-5 StartZ=0 EndX=10 EndY=-15 EndZ=0
    g63: LineSegment StartX=30 StartY=-15 StartZ=0 EndX=30 EndY=-5 EndZ=0
    g64: LineSegment StartX=50 StartY=5 StartZ=0 EndX=50 EndY=-5 EndZ=0
    g65: LineSegment StartX=70 StartY=5e-16 StartZ=0 EndX=70 EndY=10 EndZ=0
    g66: LineSegment StartX=90 StartY=5 StartZ=0 EndX=90 EndY=-5 EndZ=0
    g67: LineSegment StartX=110 StartY=-5 StartZ=0 EndX=110 EndY=5 EndZ=0
    g68: LineSegment StartX=130 StartY=5 StartZ=0 EndX=130 EndY=-5 EndZ=0
    g69: LineSegment StartX=90 StartY=-68 StartZ=0 EndX=130 EndY=-68 EndZ=0
  constraints (168):
    c: Tangent(g0,g2) = -1.5708
    c: Tangent(g2,g1) = -1.5708
    c: Tangent(g1,g3) = -1.5708
    c: Tangent(g3,g0) = -1.5708
    c: Equal(g0,g1)
    c: Vertical(g2)
    c: Tangent(g4,g6) = -1.5708
    c: Tangent(g6,g5) = -1.5708
    c: Tangent(g5,g7) = -1.5708
    c: Tangent(g7,g4) = -1.5708
    c: Equal(g4,g5)
    c: Vertical(g6)
    c: Tangent(g8,g10) = -1.5708
    c: Tangent(g10,g9) = -1.5708
    c: Tangent(g9,g11) = -1.5708
    c: Tangent(g11,g8) = -1.5708
    c: Equal(g8,g9)
    c: Vertical(g10)
    c: Tangent(g12,g14) = -1.5708
    c: Tangent(g14,g13) = -1.5708
    c: Tangent(g13,g15) = -1.5708
    c: Tangent(g15,g12) = -1.5708
    c: Equal(g12,g13)
    c: Vertical(g14)
    c: Tangent(g16,g18) = -1.5708
    c: Tangent(g18,g17) = -1.5708
    c: Tangent(g17,g19) = -1.5708
    c: Tangent(g19,g16) = -1.5708
    c: Equal(g16,g17)
    c: Vertical(g18)
    c: Tangent(g20,g22) = -1.5708
    c: Tangent(g22,g21) = -1.5708
    c: Tangent(g21,g23) = -1.5708
    c: Tangent(g23,g20) = -1.5708
    c: Equal(g20,g21)
    c: Vertical(g22)
    c: Tangent(g24,g26) = -1.5708
    c: Tangent(g26,g25) = -1.5708
    c: Tangent(g25,g27) = -1.5708
    c: Tangent(g27,g24) = -1.5708
    c: Equal(g24,g25)
    c: Vertical(g26)
    c: Tangent(g28,g30) = -1.5708
    c: Tangent(g30,g29) = -1.5708
    c: Tangent(g29,g31) = -1.5708
    c: Tangent(g31,g28) = -1.5708
    c: Equal(g28,g29)
    c: Vertical(g30)
    c: Tangent(g32,g34) = -1.5708
    c: Tangent(g34,g33) = -1.5708
    c: Tangent(g33,g35) = -1.5708
    c: Tangent(g35,g32) = -1.5708
    c: Equal(g32,g33)
    c: Vertical(g34)
    c: Tangent(g36,g38) = -1.5708
    c: Tangent(g38,g37) = -1.5708
    c: Tangent(g37,g39) = -1.5708
    c: Tangent(g39,g36) = -1.5708
    c: Equal(g36,g37)
    c: Vertical(g38)
    c: Tangent(g40,g42) = -1.5708
    c: Tangent(g42,g41) = -1.5708
    c: Tangent(g41,g43) = -1.5708
    c: Tangent(g43,g40) = -1.5708
    c: Equal(g40,g41)
    c: Vertical(g42)
    c: Tangent(g44,g46) = -1.5708
    c: Tangent(g46,g45) = -1.5708
    c: Tangent(g45,g47) = -1.5708
    c: Tangent(g47,g44) = -1.5708
    c: Equal(g44,g45)
    c: Vertical(g46)
    c: Tangent(g48,g50) = -1.5708
    c: Tangent(g50,g49) = -1.5708
    c: Tangent(g49,g51) = -1.5708
    c: Tangent(g51,g48) = -1.5708
    c: Equal(g48,g49)
    c: Vertical(g50)
    c: Tangent(g52,g54) = -1.5708
    c: Tangent(g54,g53) = -1.5708
    c: Tangent(g53,g55) = -1.5708
    c: Tangent(g55,g52) = -1.5708
    c: Equal(g52,g53)
    c: Vertical(g54)
    c: Coincident(g56,g1)
    c: Coincident(g56,g53)
    c: Coincident(g57,g53)
    c: Coincident(g57,g49)
    c: Coincident(g57,g58)
    c: Coincident(g58,g45)
    c: Coincident(g58,g59)
    c: Coincident(g59,g41)
    c: Coincident(g59,g60)
    c: Coincident(g60,g36)
    c: Coincident(g60,g61)
    c: Coincident(g61,g33)
    c: Coincident(g62,g0)
    c: Coincident(g62,g4)
    c: Vertical(g62)
    c: Coincident(g63,g9)
    c: Coincident(g63,g52)
    c: Coincident(g64,g48)
    c: Coincident(g64,g12)
    c: Coincident(g65,g17)
    c: Coincident(g65,g44)
    c: Coincident(g66,g40)
    c: Coincident(g66,g21)
    c: Coincident(g67,g24)
    c: Coincident(g67,g37)
    c: Coincident(g68,g32)
    c: Coincident(g68,g29)
    c: Vertical(g68)
    c: DistanceY(g68,g68) = 10
    c: DistanceX(g1,g1) = 4.2
    c: Equal(g1,g53)
    c: Equal(g53,g49)
    c: Equal(g49,g45)
    c: Equal(g45,g41)
    c: Equal(g41,g36)
    c: Equal(g36,g33)
    c: Equal(g5,g8)
    c: Equal(g8,g13)
    c: Equal(g13,g16)
    c: Equal(g16,g20)
    c: Equal(g20,g25)
    c: Equal(g25,g28)
    c: Equal(g5,g1)
    c: Vertical(g63)
    c: Vertical(g65)
    c: Vertical(g66)
    c: Vertical(g67)
    c: Equal(g68,g67)
    c: Equal(g67,g66)
    c: Equal(g66,g65)
    c: Equal(g65,g64)
    c: Equal(g64,g63)
    c: Equal(g63,g62)
    c: Equal(g56,g57)
    c: Equal(g57,g58)
    c: Equal(g58,g59)
    c: Equal(g59,g60)
    c: Equal(g60,g61)
    c: Horizontal(g61)
    c: Horizontal(g60)
    c: Horizontal(g59)
    c: Horizontal(g58)
    c: Horizontal(g57)
    c: Horizontal(g56)
    c: DistanceX(g-1,g0) = 10
    c: DistanceY(g-1,g45) = 65
    c: DistanceX(g56,g56) = 20
    c: Vertical(g64)
    c: DistanceY(g-1,g0) = -5
    c: DistanceY(g-1,g52) = -5
    c: DistanceY(g5,g-1) = 70
    c: DistanceY(g-1,g48) = 5
    c: DistanceY(g8,g-1) = 70
    c: DistanceY(g-1,g44) = 10
    c: DistanceY(g-1,g40) = 5
    c: DistanceY(g-1,g37) = 5
    c: Horizontal(g24,g29)
    c: DistanceY(g13,g-1) = 60
    c: DistanceY(g16,g-1) = 55
    c: DistanceY(g20,g-1) = 68  'Rlyy'
    c: Coincident(g69,g20)
    c: Horizontal(g69)
    c: Coincident(g69,g28)
    c: PointOnObject(g25,g69)
FEATURE [PartDesign::Pocket] Pocket015
  BaseFeature = -> Pad025
  Direction = (0,0,-1)
  Length = 5
  Length2 = 5
  Midplane = true
  Placement = pos=(0,0,0) rot=(1,0,0;1.5708rad)
  Profile = -> Sketch048
  ReferenceAxis = -> Sketch048 [N_Axis]
  Type = 1
FEATURE [PartDesign::Body] Body007  label="BasePlate"
  Group = -> [Sketch038,Pad024,Sketch039,Pad025,Sketch048,Pocket015]
  Origin = -> Origin007
  Tip = -> Pocket015
